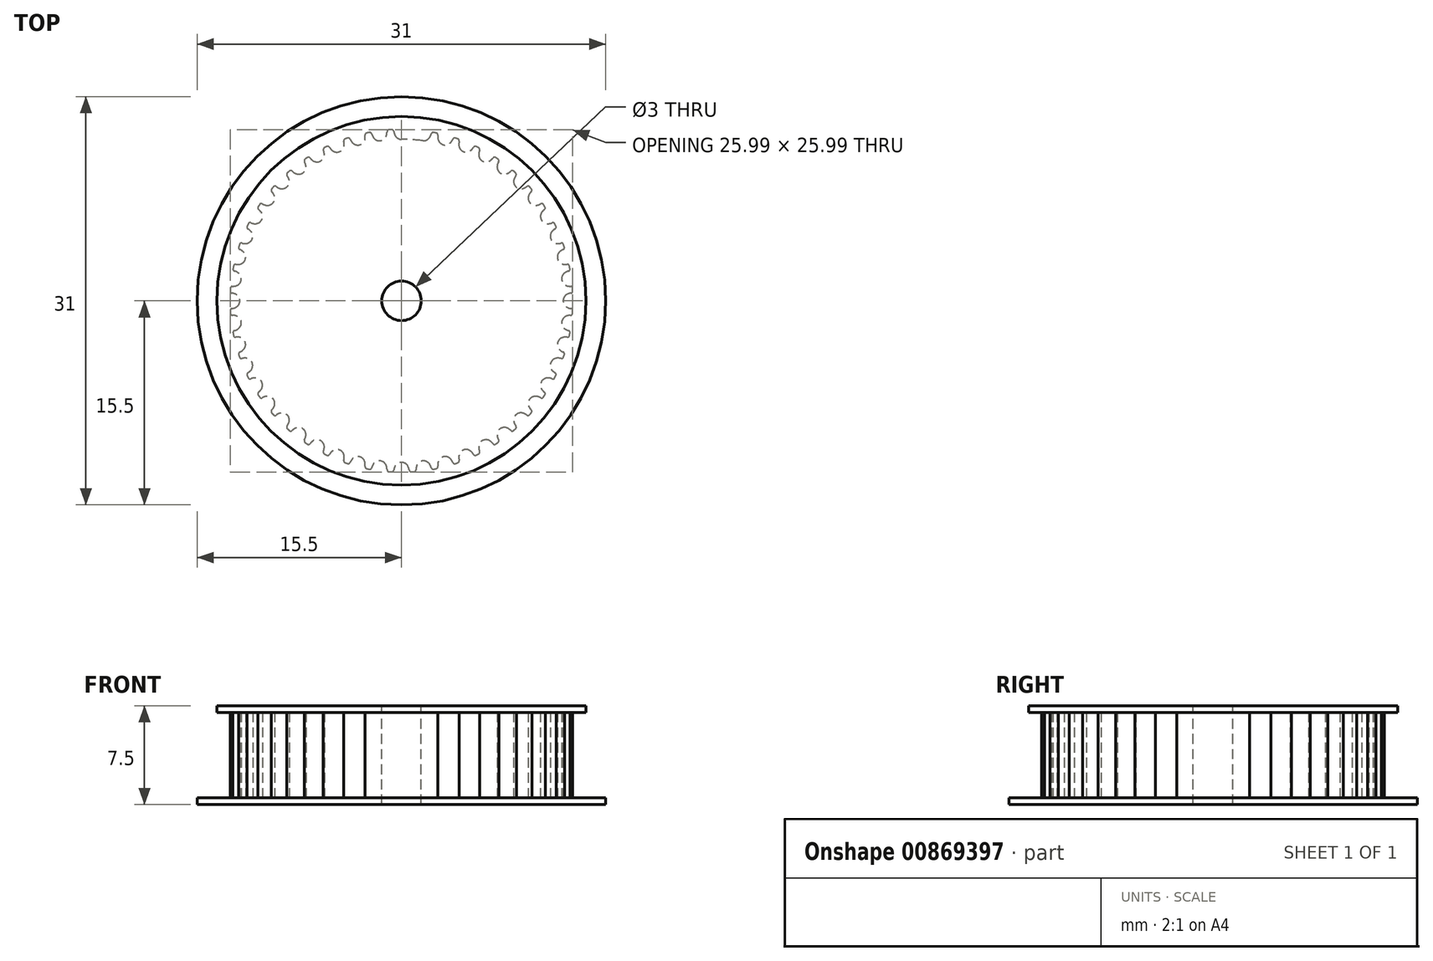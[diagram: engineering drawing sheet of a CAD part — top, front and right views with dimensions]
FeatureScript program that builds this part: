
annotation { "Feature Type Name" : "Feature", "Feature Type Description" : "" }
export const myFeature = defineFeature(function(context is Context, id is Id, definition is map)
    precondition{}
    {
        {
            var Q0;
            Q0=qCreatedBy(makeId("Top.planeOp"),FACE);
            var sketch = newSketch(context, id + "F0", { "sketchPlane" : qUnion([Q0])});
            skArc(sketch, "E0", {"start": v(-0.74, 13) * mm, "mid": v(-0.85, 12.99) * mm, "end": v(-0.96, 12.98) * mm});
            skCircle(sketch, "E1", {"center": v(0, 0) * mm, "radius": 12.27 * mm});
            skArc(sketch, "E2", {"start": v(-0.5, 12.58) * mm, "mid": v(-0.3, 12.35) * mm, "end": v(0, 12.27) * mm});
            skLineSegment(sketch, "E3", {"start": v(0, 0) * mm, "end": v(0.38, 12.26) * mm});
            skArc(sketch, "E4", {"start": v(-0.59, 12.87) * mm, "mid": v(-0.55, 12.72) * mm, "end": v(-0.5, 12.58) * mm});
            skArc(sketch, "E5", {"start": v(-0.59, 12.87) * mm, "mid": v(-0.64, 12.96) * mm, "end": v(-0.74, 13) * mm});
            skArc(sketch, "E6.MirrorCS", {"start": v(0.59, 12.87) * mm, "mid": v(0.64, 12.96) * mm, "end": v(0.74, 13) * mm});
            skArc(sketch, "E7.MirrorCS", {"start": v(0.59, 12.87) * mm, "mid": v(0.55, 12.72) * mm, "end": v(0.5, 12.58) * mm});
            skArc(sketch, "E8.MirrorCS", {"start": v(0.5, 12.58) * mm, "mid": v(0.3, 12.35) * mm, "end": v(0, 12.27) * mm});
            skArc(sketch, "E9.1.0", {"start": v(-2.26, 12.68) * mm, "mid": v(-2.33, 12.77) * mm, "end": v(-2.43, 12.79) * mm});
            skArc(sketch, "E9.1.1", {"start": v(-2.26, 12.68) * mm, "mid": v(-2.21, 12.54) * mm, "end": v(-2.14, 12.41) * mm});
            skArc(sketch, "E9.1.2", {"start": v(-2.14, 12.41) * mm, "mid": v(-1.9, 12.2) * mm, "end": v(-1.6, 12.16) * mm});
            skArc(sketch, "E9.1.3", {"start": v(-1.14, 12.54) * mm, "mid": v(-1.32, 12.28) * mm, "end": v(-1.6, 12.16) * mm});
            skArc(sketch, "E9.1.4", {"start": v(-1.1, 12.83) * mm, "mid": v(-1.11, 12.69) * mm, "end": v(-1.14, 12.54) * mm});
            skArc(sketch, "E9.1.5", {"start": v(-1.1, 12.83) * mm, "mid": v(-1.06, 12.93) * mm, "end": v(-0.96, 12.98) * mm});
            skArc(sketch, "E9.2.0", {"start": v(-3.9, 12.28) * mm, "mid": v(-3.97, 12.35) * mm, "end": v(-4.08, 12.36) * mm});
            skArc(sketch, "E9.2.1", {"start": v(-3.9, 12.28) * mm, "mid": v(-3.83, 12.14) * mm, "end": v(-3.74, 12.03) * mm});
            skArc(sketch, "E9.2.2", {"start": v(-3.74, 12.03) * mm, "mid": v(-3.48, 11.85) * mm, "end": v(-3.17, 11.85) * mm});
            skArc(sketch, "E9.2.3", {"start": v(-2.77, 12.29) * mm, "mid": v(-2.9, 12) * mm, "end": v(-3.17, 11.85) * mm});
            skArc(sketch, "E9.2.4", {"start": v(-2.76, 12.58) * mm, "mid": v(-2.76, 12.43) * mm, "end": v(-2.77, 12.29) * mm});
            skArc(sketch, "E9.2.5", {"start": v(-2.76, 12.58) * mm, "mid": v(-2.74, 12.68) * mm, "end": v(-2.64, 12.74) * mm});
            skArc(sketch, "E9.3.0", {"start": v(-5.47, 11.66) * mm, "mid": v(-5.55, 11.73) * mm, "end": v(-5.66, 11.72) * mm});
            skArc(sketch, "E9.3.1", {"start": v(-5.47, 11.66) * mm, "mid": v(-5.38, 11.54) * mm, "end": v(-5.28, 11.43) * mm});
            skArc(sketch, "E9.3.2", {"start": v(-5.28, 11.43) * mm, "mid": v(-5, 11.3) * mm, "end": v(-4.7, 11.33) * mm});
            skArc(sketch, "E9.3.3", {"start": v(-4.35, 11.82) * mm, "mid": v(-4.45, 11.53) * mm, "end": v(-4.7, 11.33) * mm});
            skArc(sketch, "E9.3.4", {"start": v(-4.38, 12.11) * mm, "mid": v(-4.36, 11.97) * mm, "end": v(-4.35, 11.82) * mm});
            skArc(sketch, "E9.3.5", {"start": v(-4.38, 12.11) * mm, "mid": v(-4.37, 12.22) * mm, "end": v(-4.29, 12.29) * mm});
            skArc(sketch, "E9.4.0", {"start": v(-6.94, 10.85) * mm, "mid": v(-7.03, 10.9) * mm, "end": v(-7.14, 10.88) * mm});
            skArc(sketch, "E9.4.1", {"start": v(-6.94, 10.85) * mm, "mid": v(-6.84, 10.74) * mm, "end": v(-6.73, 10.65) * mm});
            skArc(sketch, "E9.4.2", {"start": v(-6.73, 10.65) * mm, "mid": v(-6.43, 10.55) * mm, "end": v(-6.13, 10.62) * mm});
            skArc(sketch, "E9.4.3", {"start": v(-5.86, 11.15) * mm, "mid": v(-5.92, 10.85) * mm, "end": v(-6.13, 10.62) * mm});
            skArc(sketch, "E9.4.4", {"start": v(-5.92, 11.44) * mm, "mid": v(-5.88, 11.3) * mm, "end": v(-5.86, 11.15) * mm});
            skArc(sketch, "E9.4.5", {"start": v(-5.92, 11.44) * mm, "mid": v(-5.93, 11.54) * mm, "end": v(-5.85, 11.62) * mm});
            skArc(sketch, "E9.5.0", {"start": v(-8.3, 9.85) * mm, "mid": v(-8.4, 9.9) * mm, "end": v(-8.5, 9.86) * mm});
            skArc(sketch, "E9.5.1", {"start": v(-8.3, 9.85) * mm, "mid": v(-8.18, 9.76) * mm, "end": v(-8.06, 9.68) * mm});
            skArc(sketch, "E9.5.2", {"start": v(-8.06, 9.68) * mm, "mid": v(-7.76, 9.62) * mm, "end": v(-7.47, 9.73) * mm});
            skArc(sketch, "E9.5.3", {"start": v(-7.26, 10.29) * mm, "mid": v(-7.28, 9.98) * mm, "end": v(-7.47, 9.73) * mm});
            skArc(sketch, "E9.5.4", {"start": v(-7.37, 10.56) * mm, "mid": v(-7.3, 10.43) * mm, "end": v(-7.26, 10.29) * mm});
            skArc(sketch, "E9.5.5", {"start": v(-7.37, 10.56) * mm, "mid": v(-7.38, 10.67) * mm, "end": v(-7.32, 10.76) * mm});
            skArc(sketch, "E9.6.0", {"start": v(-9.51, 8.68) * mm, "mid": v(-9.62, 8.71) * mm, "end": v(-9.71, 8.66) * mm});
            skArc(sketch, "E9.6.1", {"start": v(-9.51, 8.68) * mm, "mid": v(-9.39, 8.6) * mm, "end": v(-9.25, 8.54) * mm});
            skArc(sketch, "E9.6.2", {"start": v(-9.25, 8.54) * mm, "mid": v(-8.94, 8.52) * mm, "end": v(-8.67, 8.67) * mm});
            skArc(sketch, "E9.6.3", {"start": v(-8.54, 9.25) * mm, "mid": v(-8.52, 8.94) * mm, "end": v(-8.67, 8.67) * mm});
            skArc(sketch, "E9.6.4", {"start": v(-8.68, 9.51) * mm, "mid": v(-8.6, 9.39) * mm, "end": v(-8.54, 9.25) * mm});
            skArc(sketch, "E9.6.5", {"start": v(-8.68, 9.51) * mm, "mid": v(-8.71, 9.62) * mm, "end": v(-8.66, 9.71) * mm});
            skArc(sketch, "E9.7.0", {"start": v(-10.56, 7.37) * mm, "mid": v(-10.67, 7.38) * mm, "end": v(-10.76, 7.32) * mm});
            skArc(sketch, "E9.7.1", {"start": v(-10.56, 7.37) * mm, "mid": v(-10.43, 7.3) * mm, "end": v(-10.29, 7.26) * mm});
            skArc(sketch, "E9.7.2", {"start": v(-10.29, 7.26) * mm, "mid": v(-9.98, 7.28) * mm, "end": v(-9.73, 7.47) * mm});
            skArc(sketch, "E9.7.3", {"start": v(-9.68, 8.06) * mm, "mid": v(-9.62, 7.76) * mm, "end": v(-9.73, 7.47) * mm});
            skArc(sketch, "E9.7.4", {"start": v(-9.85, 8.3) * mm, "mid": v(-9.76, 8.18) * mm, "end": v(-9.68, 8.06) * mm});
            skArc(sketch, "E9.7.5", {"start": v(-9.85, 8.3) * mm, "mid": v(-9.9, 8.4) * mm, "end": v(-9.86, 8.5) * mm});
            skArc(sketch, "E9.8.0", {"start": v(-11.44, 5.92) * mm, "mid": v(-11.54, 5.93) * mm, "end": v(-11.62, 5.85) * mm});
            skArc(sketch, "E9.8.1", {"start": v(-11.44, 5.92) * mm, "mid": v(-11.3, 5.88) * mm, "end": v(-11.15, 5.86) * mm});
            skArc(sketch, "E9.8.2", {"start": v(-11.15, 5.86) * mm, "mid": v(-10.85, 5.92) * mm, "end": v(-10.62, 6.13) * mm});
            skArc(sketch, "E9.8.3", {"start": v(-10.65, 6.73) * mm, "mid": v(-10.55, 6.43) * mm, "end": v(-10.62, 6.13) * mm});
            skArc(sketch, "E9.8.4", {"start": v(-10.85, 6.94) * mm, "mid": v(-10.74, 6.84) * mm, "end": v(-10.65, 6.73) * mm});
            skArc(sketch, "E9.8.5", {"start": v(-10.85, 6.94) * mm, "mid": v(-10.9, 7.03) * mm, "end": v(-10.88, 7.14) * mm});
            skArc(sketch, "E9.9.0", {"start": v(-12.11, 4.38) * mm, "mid": v(-12.22, 4.37) * mm, "end": v(-12.29, 4.29) * mm});
            skArc(sketch, "E9.9.1", {"start": v(-12.11, 4.38) * mm, "mid": v(-11.97, 4.36) * mm, "end": v(-11.82, 4.35) * mm});
            skArc(sketch, "E9.9.2", {"start": v(-11.82, 4.35) * mm, "mid": v(-11.53, 4.45) * mm, "end": v(-11.33, 4.7) * mm});
            skArc(sketch, "E9.9.3", {"start": v(-11.43, 5.28) * mm, "mid": v(-11.3, 5) * mm, "end": v(-11.33, 4.7) * mm});
            skArc(sketch, "E9.9.4", {"start": v(-11.66, 5.47) * mm, "mid": v(-11.54, 5.38) * mm, "end": v(-11.43, 5.28) * mm});
            skArc(sketch, "E9.9.5", {"start": v(-11.66, 5.47) * mm, "mid": v(-11.73, 5.55) * mm, "end": v(-11.72, 5.66) * mm});
            skArc(sketch, "E9.10.0", {"start": v(-12.58, 2.76) * mm, "mid": v(-12.68, 2.74) * mm, "end": v(-12.74, 2.64) * mm});
            skArc(sketch, "E9.10.1", {"start": v(-12.58, 2.76) * mm, "mid": v(-12.43, 2.76) * mm, "end": v(-12.29, 2.77) * mm});
            skArc(sketch, "E9.10.2", {"start": v(-12.29, 2.77) * mm, "mid": v(-12, 2.9) * mm, "end": v(-11.85, 3.17) * mm});
            skArc(sketch, "E9.10.3", {"start": v(-12.03, 3.74) * mm, "mid": v(-11.85, 3.48) * mm, "end": v(-11.85, 3.17) * mm});
            skArc(sketch, "E9.10.4", {"start": v(-12.28, 3.9) * mm, "mid": v(-12.14, 3.83) * mm, "end": v(-12.03, 3.74) * mm});
            skArc(sketch, "E9.10.5", {"start": v(-12.28, 3.9) * mm, "mid": v(-12.35, 3.97) * mm, "end": v(-12.36, 4.08) * mm});
            skArc(sketch, "E9.11.0", {"start": v(-12.83, 1.1) * mm, "mid": v(-12.93, 1.06) * mm, "end": v(-12.98, 0.96) * mm});
            skArc(sketch, "E9.11.1", {"start": v(-12.83, 1.1) * mm, "mid": v(-12.69, 1.11) * mm, "end": v(-12.54, 1.14) * mm});
            skArc(sketch, "E9.11.2", {"start": v(-12.54, 1.14) * mm, "mid": v(-12.28, 1.32) * mm, "end": v(-12.16, 1.6) * mm});
            skArc(sketch, "E9.11.3", {"start": v(-12.41, 2.14) * mm, "mid": v(-12.2, 1.9) * mm, "end": v(-12.16, 1.6) * mm});
            skArc(sketch, "E9.11.4", {"start": v(-12.68, 2.26) * mm, "mid": v(-12.54, 2.21) * mm, "end": v(-12.41, 2.14) * mm});
            skArc(sketch, "E9.11.5", {"start": v(-12.68, 2.26) * mm, "mid": v(-12.77, 2.33) * mm, "end": v(-12.79, 2.43) * mm});
            skArc(sketch, "E9.12.0", {"start": v(-12.87, -0.59) * mm, "mid": v(-12.96, -0.64) * mm, "end": v(-13, -0.74) * mm});
            skArc(sketch, "E9.12.1", {"start": v(-12.87, -0.59) * mm, "mid": v(-12.72, -0.55) * mm, "end": v(-12.58, -0.5) * mm});
            skArc(sketch, "E9.12.2", {"start": v(-12.58, -0.5) * mm, "mid": v(-12.35, -0.3) * mm, "end": v(-12.27, 0) * mm});
            skArc(sketch, "E9.12.3", {"start": v(-12.58, 0.5) * mm, "mid": v(-12.35, 0.3) * mm, "end": v(-12.27, 0) * mm});
            skArc(sketch, "E9.12.4", {"start": v(-12.87, 0.59) * mm, "mid": v(-12.72, 0.55) * mm, "end": v(-12.58, 0.5) * mm});
            skArc(sketch, "E9.12.5", {"start": v(-12.87, 0.59) * mm, "mid": v(-12.96, 0.64) * mm, "end": v(-13, 0.74) * mm});
            skArc(sketch, "E9.13.0", {"start": v(-12.68, -2.26) * mm, "mid": v(-12.77, -2.33) * mm, "end": v(-12.79, -2.43) * mm});
            skArc(sketch, "E9.13.1", {"start": v(-12.68, -2.26) * mm, "mid": v(-12.54, -2.21) * mm, "end": v(-12.41, -2.14) * mm});
            skArc(sketch, "E9.13.2", {"start": v(-12.41, -2.14) * mm, "mid": v(-12.2, -1.9) * mm, "end": v(-12.16, -1.6) * mm});
            skArc(sketch, "E9.13.3", {"start": v(-12.54, -1.14) * mm, "mid": v(-12.28, -1.32) * mm, "end": v(-12.16, -1.6) * mm});
            skArc(sketch, "E9.13.4", {"start": v(-12.83, -1.1) * mm, "mid": v(-12.69, -1.11) * mm, "end": v(-12.54, -1.14) * mm});
            skArc(sketch, "E9.13.5", {"start": v(-12.83, -1.1) * mm, "mid": v(-12.93, -1.06) * mm, "end": v(-12.98, -0.96) * mm});
            skArc(sketch, "E9.14.0", {"start": v(-12.28, -3.9) * mm, "mid": v(-12.35, -3.97) * mm, "end": v(-12.36, -4.08) * mm});
            skArc(sketch, "E9.14.1", {"start": v(-12.28, -3.9) * mm, "mid": v(-12.14, -3.83) * mm, "end": v(-12.03, -3.74) * mm});
            skArc(sketch, "E9.14.2", {"start": v(-12.03, -3.74) * mm, "mid": v(-11.85, -3.48) * mm, "end": v(-11.85, -3.17) * mm});
            skArc(sketch, "E9.14.3", {"start": v(-12.29, -2.77) * mm, "mid": v(-12, -2.9) * mm, "end": v(-11.85, -3.17) * mm});
            skArc(sketch, "E9.14.4", {"start": v(-12.58, -2.76) * mm, "mid": v(-12.43, -2.76) * mm, "end": v(-12.29, -2.77) * mm});
            skArc(sketch, "E9.14.5", {"start": v(-12.58, -2.76) * mm, "mid": v(-12.68, -2.74) * mm, "end": v(-12.74, -2.64) * mm});
            skArc(sketch, "E9.15.0", {"start": v(-11.66, -5.47) * mm, "mid": v(-11.73, -5.55) * mm, "end": v(-11.72, -5.66) * mm});
            skArc(sketch, "E9.15.1", {"start": v(-11.66, -5.47) * mm, "mid": v(-11.54, -5.38) * mm, "end": v(-11.43, -5.28) * mm});
            skArc(sketch, "E9.15.2", {"start": v(-11.43, -5.28) * mm, "mid": v(-11.3, -5) * mm, "end": v(-11.33, -4.7) * mm});
            skArc(sketch, "E9.15.3", {"start": v(-11.82, -4.35) * mm, "mid": v(-11.53, -4.45) * mm, "end": v(-11.33, -4.7) * mm});
            skArc(sketch, "E9.15.4", {"start": v(-12.11, -4.38) * mm, "mid": v(-11.97, -4.36) * mm, "end": v(-11.82, -4.35) * mm});
            skArc(sketch, "E9.15.5", {"start": v(-12.11, -4.38) * mm, "mid": v(-12.22, -4.37) * mm, "end": v(-12.29, -4.29) * mm});
            skArc(sketch, "E9.16.0", {"start": v(-10.85, -6.94) * mm, "mid": v(-10.9, -7.03) * mm, "end": v(-10.88, -7.14) * mm});
            skArc(sketch, "E9.16.1", {"start": v(-10.85, -6.94) * mm, "mid": v(-10.74, -6.84) * mm, "end": v(-10.65, -6.73) * mm});
            skArc(sketch, "E9.16.2", {"start": v(-10.65, -6.73) * mm, "mid": v(-10.55, -6.43) * mm, "end": v(-10.62, -6.13) * mm});
            skArc(sketch, "E9.16.3", {"start": v(-11.15, -5.86) * mm, "mid": v(-10.85, -5.92) * mm, "end": v(-10.62, -6.13) * mm});
            skArc(sketch, "E9.16.4", {"start": v(-11.44, -5.92) * mm, "mid": v(-11.3, -5.88) * mm, "end": v(-11.15, -5.86) * mm});
            skArc(sketch, "E9.16.5", {"start": v(-11.44, -5.92) * mm, "mid": v(-11.54, -5.93) * mm, "end": v(-11.62, -5.85) * mm});
            skArc(sketch, "E9.17.0", {"start": v(-9.85, -8.3) * mm, "mid": v(-9.9, -8.4) * mm, "end": v(-9.86, -8.5) * mm});
            skArc(sketch, "E9.17.1", {"start": v(-9.85, -8.3) * mm, "mid": v(-9.76, -8.18) * mm, "end": v(-9.68, -8.06) * mm});
            skArc(sketch, "E9.17.2", {"start": v(-9.68, -8.06) * mm, "mid": v(-9.62, -7.76) * mm, "end": v(-9.73, -7.47) * mm});
            skArc(sketch, "E9.17.3", {"start": v(-10.29, -7.26) * mm, "mid": v(-9.98, -7.28) * mm, "end": v(-9.73, -7.47) * mm});
            skArc(sketch, "E9.17.4", {"start": v(-10.56, -7.37) * mm, "mid": v(-10.43, -7.3) * mm, "end": v(-10.29, -7.26) * mm});
            skArc(sketch, "E9.17.5", {"start": v(-10.56, -7.37) * mm, "mid": v(-10.67, -7.38) * mm, "end": v(-10.76, -7.32) * mm});
            skArc(sketch, "E9.18.0", {"start": v(-8.68, -9.51) * mm, "mid": v(-8.71, -9.62) * mm, "end": v(-8.66, -9.71) * mm});
            skArc(sketch, "E9.18.1", {"start": v(-8.68, -9.51) * mm, "mid": v(-8.6, -9.39) * mm, "end": v(-8.54, -9.25) * mm});
            skArc(sketch, "E9.18.2", {"start": v(-8.54, -9.25) * mm, "mid": v(-8.52, -8.94) * mm, "end": v(-8.67, -8.67) * mm});
            skArc(sketch, "E9.18.3", {"start": v(-9.25, -8.54) * mm, "mid": v(-8.94, -8.52) * mm, "end": v(-8.67, -8.67) * mm});
            skArc(sketch, "E9.18.4", {"start": v(-9.51, -8.68) * mm, "mid": v(-9.39, -8.6) * mm, "end": v(-9.25, -8.54) * mm});
            skArc(sketch, "E9.18.5", {"start": v(-9.51, -8.68) * mm, "mid": v(-9.62, -8.71) * mm, "end": v(-9.71, -8.66) * mm});
            skArc(sketch, "E9.19.0", {"start": v(-7.37, -10.56) * mm, "mid": v(-7.38, -10.67) * mm, "end": v(-7.32, -10.76) * mm});
            skArc(sketch, "E9.19.1", {"start": v(-7.37, -10.56) * mm, "mid": v(-7.3, -10.43) * mm, "end": v(-7.26, -10.29) * mm});
            skArc(sketch, "E9.19.2", {"start": v(-7.26, -10.29) * mm, "mid": v(-7.28, -9.98) * mm, "end": v(-7.47, -9.73) * mm});
            skArc(sketch, "E9.19.3", {"start": v(-8.06, -9.68) * mm, "mid": v(-7.76, -9.62) * mm, "end": v(-7.47, -9.73) * mm});
            skArc(sketch, "E9.19.4", {"start": v(-8.3, -9.85) * mm, "mid": v(-8.18, -9.76) * mm, "end": v(-8.06, -9.68) * mm});
            skArc(sketch, "E9.19.5", {"start": v(-8.3, -9.85) * mm, "mid": v(-8.4, -9.9) * mm, "end": v(-8.5, -9.86) * mm});
            skArc(sketch, "E9.20.0", {"start": v(-5.92, -11.44) * mm, "mid": v(-5.93, -11.54) * mm, "end": v(-5.85, -11.62) * mm});
            skArc(sketch, "E9.20.1", {"start": v(-5.92, -11.44) * mm, "mid": v(-5.88, -11.3) * mm, "end": v(-5.86, -11.15) * mm});
            skArc(sketch, "E9.20.2", {"start": v(-5.86, -11.15) * mm, "mid": v(-5.92, -10.85) * mm, "end": v(-6.13, -10.62) * mm});
            skArc(sketch, "E9.20.3", {"start": v(-6.73, -10.65) * mm, "mid": v(-6.43, -10.55) * mm, "end": v(-6.13, -10.62) * mm});
            skArc(sketch, "E9.20.4", {"start": v(-6.94, -10.85) * mm, "mid": v(-6.84, -10.74) * mm, "end": v(-6.73, -10.65) * mm});
            skArc(sketch, "E9.20.5", {"start": v(-6.94, -10.85) * mm, "mid": v(-7.03, -10.9) * mm, "end": v(-7.14, -10.88) * mm});
            skArc(sketch, "E9.21.0", {"start": v(-4.38, -12.11) * mm, "mid": v(-4.37, -12.22) * mm, "end": v(-4.29, -12.29) * mm});
            skArc(sketch, "E9.21.1", {"start": v(-4.38, -12.11) * mm, "mid": v(-4.36, -11.97) * mm, "end": v(-4.35, -11.82) * mm});
            skArc(sketch, "E9.21.2", {"start": v(-4.35, -11.82) * mm, "mid": v(-4.45, -11.53) * mm, "end": v(-4.7, -11.33) * mm});
            skArc(sketch, "E9.21.3", {"start": v(-5.28, -11.43) * mm, "mid": v(-5, -11.3) * mm, "end": v(-4.7, -11.33) * mm});
            skArc(sketch, "E9.21.4", {"start": v(-5.47, -11.66) * mm, "mid": v(-5.38, -11.54) * mm, "end": v(-5.28, -11.43) * mm});
            skArc(sketch, "E9.21.5", {"start": v(-5.47, -11.66) * mm, "mid": v(-5.55, -11.73) * mm, "end": v(-5.66, -11.72) * mm});
            skArc(sketch, "E9.22.0", {"start": v(-2.76, -12.58) * mm, "mid": v(-2.74, -12.68) * mm, "end": v(-2.64, -12.74) * mm});
            skArc(sketch, "E9.22.1", {"start": v(-2.76, -12.58) * mm, "mid": v(-2.76, -12.43) * mm, "end": v(-2.77, -12.29) * mm});
            skArc(sketch, "E9.22.2", {"start": v(-2.77, -12.29) * mm, "mid": v(-2.9, -12) * mm, "end": v(-3.17, -11.85) * mm});
            skArc(sketch, "E9.22.3", {"start": v(-3.74, -12.03) * mm, "mid": v(-3.48, -11.85) * mm, "end": v(-3.17, -11.85) * mm});
            skArc(sketch, "E9.22.4", {"start": v(-3.9, -12.28) * mm, "mid": v(-3.83, -12.14) * mm, "end": v(-3.74, -12.03) * mm});
            skArc(sketch, "E9.22.5", {"start": v(-3.9, -12.28) * mm, "mid": v(-3.97, -12.35) * mm, "end": v(-4.08, -12.36) * mm});
            skArc(sketch, "E9.23.0", {"start": v(-1.1, -12.83) * mm, "mid": v(-1.06, -12.93) * mm, "end": v(-0.96, -12.98) * mm});
            skArc(sketch, "E9.23.1", {"start": v(-1.1, -12.83) * mm, "mid": v(-1.11, -12.69) * mm, "end": v(-1.14, -12.54) * mm});
            skArc(sketch, "E9.23.2", {"start": v(-1.14, -12.54) * mm, "mid": v(-1.32, -12.28) * mm, "end": v(-1.6, -12.16) * mm});
            skArc(sketch, "E9.23.3", {"start": v(-2.14, -12.41) * mm, "mid": v(-1.9, -12.2) * mm, "end": v(-1.6, -12.16) * mm});
            skArc(sketch, "E9.23.4", {"start": v(-2.26, -12.68) * mm, "mid": v(-2.21, -12.54) * mm, "end": v(-2.14, -12.41) * mm});
            skArc(sketch, "E9.23.5", {"start": v(-2.26, -12.68) * mm, "mid": v(-2.33, -12.77) * mm, "end": v(-2.43, -12.79) * mm});
            skArc(sketch, "E9.24.0", {"start": v(0.59, -12.87) * mm, "mid": v(0.64, -12.96) * mm, "end": v(0.74, -13) * mm});
            skArc(sketch, "E9.24.1", {"start": v(0.59, -12.87) * mm, "mid": v(0.55, -12.72) * mm, "end": v(0.5, -12.58) * mm});
            skArc(sketch, "E9.24.2", {"start": v(0.5, -12.58) * mm, "mid": v(0.3, -12.35) * mm, "end": v(0, -12.27) * mm});
            skArc(sketch, "E9.24.3", {"start": v(-0.5, -12.58) * mm, "mid": v(-0.3, -12.35) * mm, "end": v(0, -12.27) * mm});
            skArc(sketch, "E9.24.4", {"start": v(-0.59, -12.87) * mm, "mid": v(-0.55, -12.72) * mm, "end": v(-0.5, -12.58) * mm});
            skArc(sketch, "E9.24.5", {"start": v(-0.59, -12.87) * mm, "mid": v(-0.64, -12.96) * mm, "end": v(-0.74, -13) * mm});
            skArc(sketch, "E9.25.0", {"start": v(2.26, -12.68) * mm, "mid": v(2.33, -12.77) * mm, "end": v(2.43, -12.79) * mm});
            skArc(sketch, "E9.25.1", {"start": v(2.26, -12.68) * mm, "mid": v(2.21, -12.54) * mm, "end": v(2.14, -12.41) * mm});
            skArc(sketch, "E9.25.2", {"start": v(2.14, -12.41) * mm, "mid": v(1.9, -12.2) * mm, "end": v(1.6, -12.16) * mm});
            skArc(sketch, "E9.25.3", {"start": v(1.14, -12.54) * mm, "mid": v(1.32, -12.28) * mm, "end": v(1.6, -12.16) * mm});
            skArc(sketch, "E9.25.4", {"start": v(1.1, -12.83) * mm, "mid": v(1.11, -12.69) * mm, "end": v(1.14, -12.54) * mm});
            skArc(sketch, "E9.25.5", {"start": v(1.1, -12.83) * mm, "mid": v(1.06, -12.93) * mm, "end": v(0.96, -12.98) * mm});
            skArc(sketch, "E9.26.0", {"start": v(3.9, -12.28) * mm, "mid": v(3.97, -12.35) * mm, "end": v(4.08, -12.36) * mm});
            skArc(sketch, "E9.26.1", {"start": v(3.9, -12.28) * mm, "mid": v(3.83, -12.14) * mm, "end": v(3.74, -12.03) * mm});
            skArc(sketch, "E9.26.2", {"start": v(3.74, -12.03) * mm, "mid": v(3.48, -11.85) * mm, "end": v(3.17, -11.85) * mm});
            skArc(sketch, "E9.26.3", {"start": v(2.77, -12.29) * mm, "mid": v(2.9, -12) * mm, "end": v(3.17, -11.85) * mm});
            skArc(sketch, "E9.26.4", {"start": v(2.76, -12.58) * mm, "mid": v(2.76, -12.43) * mm, "end": v(2.77, -12.29) * mm});
            skArc(sketch, "E9.26.5", {"start": v(2.76, -12.58) * mm, "mid": v(2.74, -12.68) * mm, "end": v(2.64, -12.74) * mm});
            skArc(sketch, "E9.27.0", {"start": v(5.47, -11.66) * mm, "mid": v(5.55, -11.73) * mm, "end": v(5.66, -11.72) * mm});
            skArc(sketch, "E9.27.1", {"start": v(5.47, -11.66) * mm, "mid": v(5.38, -11.54) * mm, "end": v(5.28, -11.43) * mm});
            skArc(sketch, "E9.27.2", {"start": v(5.28, -11.43) * mm, "mid": v(5, -11.3) * mm, "end": v(4.7, -11.33) * mm});
            skArc(sketch, "E9.27.3", {"start": v(4.35, -11.82) * mm, "mid": v(4.45, -11.53) * mm, "end": v(4.7, -11.33) * mm});
            skArc(sketch, "E9.27.4", {"start": v(4.38, -12.11) * mm, "mid": v(4.36, -11.97) * mm, "end": v(4.35, -11.82) * mm});
            skArc(sketch, "E9.27.5", {"start": v(4.38, -12.11) * mm, "mid": v(4.37, -12.22) * mm, "end": v(4.29, -12.29) * mm});
            skArc(sketch, "E9.28.0", {"start": v(6.94, -10.85) * mm, "mid": v(7.03, -10.9) * mm, "end": v(7.14, -10.88) * mm});
            skArc(sketch, "E9.28.1", {"start": v(6.94, -10.85) * mm, "mid": v(6.84, -10.74) * mm, "end": v(6.73, -10.65) * mm});
            skArc(sketch, "E9.28.2", {"start": v(6.73, -10.65) * mm, "mid": v(6.43, -10.55) * mm, "end": v(6.13, -10.62) * mm});
            skArc(sketch, "E9.28.3", {"start": v(5.86, -11.15) * mm, "mid": v(5.92, -10.85) * mm, "end": v(6.13, -10.62) * mm});
            skArc(sketch, "E9.28.4", {"start": v(5.92, -11.44) * mm, "mid": v(5.88, -11.3) * mm, "end": v(5.86, -11.15) * mm});
            skArc(sketch, "E9.28.5", {"start": v(5.92, -11.44) * mm, "mid": v(5.93, -11.54) * mm, "end": v(5.85, -11.62) * mm});
            skArc(sketch, "E9.29.0", {"start": v(8.3, -9.85) * mm, "mid": v(8.4, -9.9) * mm, "end": v(8.5, -9.86) * mm});
            skArc(sketch, "E9.29.1", {"start": v(8.3, -9.85) * mm, "mid": v(8.18, -9.76) * mm, "end": v(8.06, -9.68) * mm});
            skArc(sketch, "E9.29.2", {"start": v(8.06, -9.68) * mm, "mid": v(7.76, -9.62) * mm, "end": v(7.47, -9.73) * mm});
            skArc(sketch, "E9.29.3", {"start": v(7.26, -10.29) * mm, "mid": v(7.28, -9.98) * mm, "end": v(7.47, -9.73) * mm});
            skArc(sketch, "E9.29.4", {"start": v(7.37, -10.56) * mm, "mid": v(7.3, -10.43) * mm, "end": v(7.26, -10.29) * mm});
            skArc(sketch, "E9.29.5", {"start": v(7.37, -10.56) * mm, "mid": v(7.38, -10.67) * mm, "end": v(7.32, -10.76) * mm});
            skArc(sketch, "E9.30.0", {"start": v(9.51, -8.68) * mm, "mid": v(9.62, -8.71) * mm, "end": v(9.71, -8.66) * mm});
            skArc(sketch, "E9.30.1", {"start": v(9.51, -8.68) * mm, "mid": v(9.39, -8.6) * mm, "end": v(9.25, -8.54) * mm});
            skArc(sketch, "E9.30.2", {"start": v(9.25, -8.54) * mm, "mid": v(8.94, -8.52) * mm, "end": v(8.67, -8.67) * mm});
            skArc(sketch, "E9.30.3", {"start": v(8.54, -9.25) * mm, "mid": v(8.52, -8.94) * mm, "end": v(8.67, -8.67) * mm});
            skArc(sketch, "E9.30.4", {"start": v(8.68, -9.51) * mm, "mid": v(8.6, -9.39) * mm, "end": v(8.54, -9.25) * mm});
            skArc(sketch, "E9.30.5", {"start": v(8.68, -9.51) * mm, "mid": v(8.71, -9.62) * mm, "end": v(8.66, -9.71) * mm});
            skArc(sketch, "E9.31.0", {"start": v(10.56, -7.37) * mm, "mid": v(10.67, -7.38) * mm, "end": v(10.76, -7.32) * mm});
            skArc(sketch, "E9.31.1", {"start": v(10.56, -7.37) * mm, "mid": v(10.43, -7.3) * mm, "end": v(10.29, -7.26) * mm});
            skArc(sketch, "E9.31.2", {"start": v(10.29, -7.26) * mm, "mid": v(9.98, -7.28) * mm, "end": v(9.73, -7.47) * mm});
            skArc(sketch, "E9.31.3", {"start": v(9.68, -8.06) * mm, "mid": v(9.62, -7.76) * mm, "end": v(9.73, -7.47) * mm});
            skArc(sketch, "E9.31.4", {"start": v(9.85, -8.3) * mm, "mid": v(9.76, -8.18) * mm, "end": v(9.68, -8.06) * mm});
            skArc(sketch, "E9.31.5", {"start": v(9.85, -8.3) * mm, "mid": v(9.9, -8.4) * mm, "end": v(9.86, -8.5) * mm});
            skArc(sketch, "E9.32.0", {"start": v(11.44, -5.92) * mm, "mid": v(11.54, -5.93) * mm, "end": v(11.62, -5.85) * mm});
            skArc(sketch, "E9.32.1", {"start": v(11.44, -5.92) * mm, "mid": v(11.3, -5.88) * mm, "end": v(11.15, -5.86) * mm});
            skArc(sketch, "E9.32.2", {"start": v(11.15, -5.86) * mm, "mid": v(10.85, -5.92) * mm, "end": v(10.62, -6.13) * mm});
            skArc(sketch, "E9.32.3", {"start": v(10.65, -6.73) * mm, "mid": v(10.55, -6.43) * mm, "end": v(10.62, -6.13) * mm});
            skArc(sketch, "E9.32.4", {"start": v(10.85, -6.94) * mm, "mid": v(10.74, -6.84) * mm, "end": v(10.65, -6.73) * mm});
            skArc(sketch, "E9.32.5", {"start": v(10.85, -6.94) * mm, "mid": v(10.9, -7.03) * mm, "end": v(10.88, -7.14) * mm});
            skArc(sketch, "E9.33.0", {"start": v(12.11, -4.38) * mm, "mid": v(12.22, -4.37) * mm, "end": v(12.29, -4.29) * mm});
            skArc(sketch, "E9.33.1", {"start": v(12.11, -4.38) * mm, "mid": v(11.97, -4.36) * mm, "end": v(11.82, -4.35) * mm});
            skArc(sketch, "E9.33.2", {"start": v(11.82, -4.35) * mm, "mid": v(11.53, -4.45) * mm, "end": v(11.33, -4.7) * mm});
            skArc(sketch, "E9.33.3", {"start": v(11.43, -5.28) * mm, "mid": v(11.3, -5) * mm, "end": v(11.33, -4.7) * mm});
            skArc(sketch, "E9.33.4", {"start": v(11.66, -5.47) * mm, "mid": v(11.54, -5.38) * mm, "end": v(11.43, -5.28) * mm});
            skArc(sketch, "E9.33.5", {"start": v(11.66, -5.47) * mm, "mid": v(11.73, -5.55) * mm, "end": v(11.72, -5.66) * mm});
            skArc(sketch, "E9.34.0", {"start": v(12.58, -2.76) * mm, "mid": v(12.68, -2.74) * mm, "end": v(12.74, -2.64) * mm});
            skArc(sketch, "E9.34.1", {"start": v(12.58, -2.76) * mm, "mid": v(12.43, -2.76) * mm, "end": v(12.29, -2.77) * mm});
            skArc(sketch, "E9.34.2", {"start": v(12.29, -2.77) * mm, "mid": v(12, -2.9) * mm, "end": v(11.85, -3.17) * mm});
            skArc(sketch, "E9.34.3", {"start": v(12.03, -3.74) * mm, "mid": v(11.85, -3.48) * mm, "end": v(11.85, -3.17) * mm});
            skArc(sketch, "E9.34.4", {"start": v(12.28, -3.9) * mm, "mid": v(12.14, -3.83) * mm, "end": v(12.03, -3.74) * mm});
            skArc(sketch, "E9.34.5", {"start": v(12.28, -3.9) * mm, "mid": v(12.35, -3.97) * mm, "end": v(12.36, -4.08) * mm});
            skArc(sketch, "E9.35.0", {"start": v(12.83, -1.1) * mm, "mid": v(12.93, -1.06) * mm, "end": v(12.98, -0.96) * mm});
            skArc(sketch, "E9.35.1", {"start": v(12.83, -1.1) * mm, "mid": v(12.69, -1.11) * mm, "end": v(12.54, -1.14) * mm});
            skArc(sketch, "E9.35.2", {"start": v(12.54, -1.14) * mm, "mid": v(12.28, -1.32) * mm, "end": v(12.16, -1.6) * mm});
            skArc(sketch, "E9.35.3", {"start": v(12.41, -2.14) * mm, "mid": v(12.2, -1.9) * mm, "end": v(12.16, -1.6) * mm});
            skArc(sketch, "E9.35.4", {"start": v(12.68, -2.26) * mm, "mid": v(12.54, -2.21) * mm, "end": v(12.41, -2.14) * mm});
            skArc(sketch, "E9.35.5", {"start": v(12.68, -2.26) * mm, "mid": v(12.77, -2.33) * mm, "end": v(12.79, -2.43) * mm});
            skArc(sketch, "E9.36.0", {"start": v(12.87, 0.59) * mm, "mid": v(12.96, 0.64) * mm, "end": v(13, 0.74) * mm});
            skArc(sketch, "E9.36.1", {"start": v(12.87, 0.59) * mm, "mid": v(12.72, 0.55) * mm, "end": v(12.58, 0.5) * mm});
            skArc(sketch, "E9.36.2", {"start": v(12.58, 0.5) * mm, "mid": v(12.35, 0.3) * mm, "end": v(12.27, 0) * mm});
            skArc(sketch, "E9.36.3", {"start": v(12.58, -0.5) * mm, "mid": v(12.35, -0.3) * mm, "end": v(12.27, 0) * mm});
            skArc(sketch, "E9.36.4", {"start": v(12.87, -0.59) * mm, "mid": v(12.72, -0.55) * mm, "end": v(12.58, -0.5) * mm});
            skArc(sketch, "E9.36.5", {"start": v(12.87, -0.59) * mm, "mid": v(12.96, -0.64) * mm, "end": v(13, -0.74) * mm});
            skArc(sketch, "E9.37.0", {"start": v(12.68, 2.26) * mm, "mid": v(12.77, 2.33) * mm, "end": v(12.79, 2.43) * mm});
            skArc(sketch, "E9.37.1", {"start": v(12.68, 2.26) * mm, "mid": v(12.54, 2.21) * mm, "end": v(12.41, 2.14) * mm});
            skArc(sketch, "E9.37.2", {"start": v(12.41, 2.14) * mm, "mid": v(12.2, 1.9) * mm, "end": v(12.16, 1.6) * mm});
            skArc(sketch, "E9.37.3", {"start": v(12.54, 1.14) * mm, "mid": v(12.28, 1.32) * mm, "end": v(12.16, 1.6) * mm});
            skArc(sketch, "E9.37.4", {"start": v(12.83, 1.1) * mm, "mid": v(12.69, 1.11) * mm, "end": v(12.54, 1.14) * mm});
            skArc(sketch, "E9.37.5", {"start": v(12.83, 1.1) * mm, "mid": v(12.93, 1.06) * mm, "end": v(12.98, 0.96) * mm});
            skArc(sketch, "E9.38.0", {"start": v(12.28, 3.9) * mm, "mid": v(12.35, 3.97) * mm, "end": v(12.36, 4.08) * mm});
            skArc(sketch, "E9.38.1", {"start": v(12.28, 3.9) * mm, "mid": v(12.14, 3.83) * mm, "end": v(12.03, 3.74) * mm});
            skArc(sketch, "E9.38.2", {"start": v(12.03, 3.74) * mm, "mid": v(11.85, 3.48) * mm, "end": v(11.85, 3.17) * mm});
            skArc(sketch, "E9.38.3", {"start": v(12.29, 2.77) * mm, "mid": v(12, 2.9) * mm, "end": v(11.85, 3.17) * mm});
            skArc(sketch, "E9.38.4", {"start": v(12.58, 2.76) * mm, "mid": v(12.43, 2.76) * mm, "end": v(12.29, 2.77) * mm});
            skArc(sketch, "E9.38.5", {"start": v(12.58, 2.76) * mm, "mid": v(12.68, 2.74) * mm, "end": v(12.74, 2.64) * mm});
            skArc(sketch, "E9.39.0", {"start": v(11.66, 5.47) * mm, "mid": v(11.73, 5.55) * mm, "end": v(11.72, 5.66) * mm});
            skArc(sketch, "E9.39.1", {"start": v(11.66, 5.47) * mm, "mid": v(11.54, 5.38) * mm, "end": v(11.43, 5.28) * mm});
            skArc(sketch, "E9.39.2", {"start": v(11.43, 5.28) * mm, "mid": v(11.3, 5) * mm, "end": v(11.33, 4.7) * mm});
            skArc(sketch, "E9.39.3", {"start": v(11.82, 4.35) * mm, "mid": v(11.53, 4.45) * mm, "end": v(11.33, 4.7) * mm});
            skArc(sketch, "E9.39.4", {"start": v(12.11, 4.38) * mm, "mid": v(11.97, 4.36) * mm, "end": v(11.82, 4.35) * mm});
            skArc(sketch, "E9.39.5", {"start": v(12.11, 4.38) * mm, "mid": v(12.22, 4.37) * mm, "end": v(12.29, 4.29) * mm});
            skArc(sketch, "E9.40.0", {"start": v(10.85, 6.94) * mm, "mid": v(10.9, 7.03) * mm, "end": v(10.88, 7.14) * mm});
            skArc(sketch, "E9.40.1", {"start": v(10.85, 6.94) * mm, "mid": v(10.74, 6.84) * mm, "end": v(10.65, 6.73) * mm});
            skArc(sketch, "E9.40.2", {"start": v(10.65, 6.73) * mm, "mid": v(10.55, 6.43) * mm, "end": v(10.62, 6.13) * mm});
            skArc(sketch, "E9.40.3", {"start": v(11.15, 5.86) * mm, "mid": v(10.85, 5.92) * mm, "end": v(10.62, 6.13) * mm});
            skArc(sketch, "E9.40.4", {"start": v(11.44, 5.92) * mm, "mid": v(11.3, 5.88) * mm, "end": v(11.15, 5.86) * mm});
            skArc(sketch, "E9.40.5", {"start": v(11.44, 5.92) * mm, "mid": v(11.54, 5.93) * mm, "end": v(11.62, 5.85) * mm});
            skArc(sketch, "E9.41.0", {"start": v(9.85, 8.3) * mm, "mid": v(9.9, 8.4) * mm, "end": v(9.86, 8.5) * mm});
            skArc(sketch, "E9.41.1", {"start": v(9.85, 8.3) * mm, "mid": v(9.76, 8.18) * mm, "end": v(9.68, 8.06) * mm});
            skArc(sketch, "E9.41.2", {"start": v(9.68, 8.06) * mm, "mid": v(9.62, 7.76) * mm, "end": v(9.73, 7.47) * mm});
            skArc(sketch, "E9.41.3", {"start": v(10.29, 7.26) * mm, "mid": v(9.98, 7.28) * mm, "end": v(9.73, 7.47) * mm});
            skArc(sketch, "E9.41.4", {"start": v(10.56, 7.37) * mm, "mid": v(10.43, 7.3) * mm, "end": v(10.29, 7.26) * mm});
            skArc(sketch, "E9.41.5", {"start": v(10.56, 7.37) * mm, "mid": v(10.67, 7.38) * mm, "end": v(10.76, 7.32) * mm});
            skArc(sketch, "E9.42.0", {"start": v(8.68, 9.51) * mm, "mid": v(8.71, 9.62) * mm, "end": v(8.66, 9.71) * mm});
            skArc(sketch, "E9.42.1", {"start": v(8.68, 9.51) * mm, "mid": v(8.6, 9.39) * mm, "end": v(8.54, 9.25) * mm});
            skArc(sketch, "E9.42.2", {"start": v(8.54, 9.25) * mm, "mid": v(8.52, 8.94) * mm, "end": v(8.67, 8.67) * mm});
            skArc(sketch, "E9.42.3", {"start": v(9.25, 8.54) * mm, "mid": v(8.94, 8.52) * mm, "end": v(8.67, 8.67) * mm});
            skArc(sketch, "E9.42.4", {"start": v(9.51, 8.68) * mm, "mid": v(9.39, 8.6) * mm, "end": v(9.25, 8.54) * mm});
            skArc(sketch, "E9.42.5", {"start": v(9.51, 8.68) * mm, "mid": v(9.62, 8.71) * mm, "end": v(9.71, 8.66) * mm});
            skArc(sketch, "E9.43.0", {"start": v(7.37, 10.56) * mm, "mid": v(7.38, 10.67) * mm, "end": v(7.32, 10.76) * mm});
            skArc(sketch, "E9.43.1", {"start": v(7.37, 10.56) * mm, "mid": v(7.3, 10.43) * mm, "end": v(7.26, 10.29) * mm});
            skArc(sketch, "E9.43.2", {"start": v(7.26, 10.29) * mm, "mid": v(7.28, 9.98) * mm, "end": v(7.47, 9.73) * mm});
            skArc(sketch, "E9.43.3", {"start": v(8.06, 9.68) * mm, "mid": v(7.76, 9.62) * mm, "end": v(7.47, 9.73) * mm});
            skArc(sketch, "E9.43.4", {"start": v(8.3, 9.85) * mm, "mid": v(8.18, 9.76) * mm, "end": v(8.06, 9.68) * mm});
            skArc(sketch, "E9.43.5", {"start": v(8.3, 9.85) * mm, "mid": v(8.4, 9.9) * mm, "end": v(8.5, 9.86) * mm});
            skArc(sketch, "E9.44.0", {"start": v(5.92, 11.44) * mm, "mid": v(5.93, 11.54) * mm, "end": v(5.85, 11.62) * mm});
            skArc(sketch, "E9.44.1", {"start": v(5.92, 11.44) * mm, "mid": v(5.88, 11.3) * mm, "end": v(5.86, 11.15) * mm});
            skArc(sketch, "E9.44.2", {"start": v(5.86, 11.15) * mm, "mid": v(5.92, 10.85) * mm, "end": v(6.13, 10.62) * mm});
            skArc(sketch, "E9.44.3", {"start": v(6.73, 10.65) * mm, "mid": v(6.43, 10.55) * mm, "end": v(6.13, 10.62) * mm});
            skArc(sketch, "E9.44.4", {"start": v(6.94, 10.85) * mm, "mid": v(6.84, 10.74) * mm, "end": v(6.73, 10.65) * mm});
            skArc(sketch, "E9.44.5", {"start": v(6.94, 10.85) * mm, "mid": v(7.03, 10.9) * mm, "end": v(7.14, 10.88) * mm});
            skArc(sketch, "E9.45.0", {"start": v(4.38, 12.11) * mm, "mid": v(4.37, 12.22) * mm, "end": v(4.29, 12.29) * mm});
            skArc(sketch, "E9.45.1", {"start": v(4.38, 12.11) * mm, "mid": v(4.36, 11.97) * mm, "end": v(4.35, 11.82) * mm});
            skArc(sketch, "E9.45.2", {"start": v(4.35, 11.82) * mm, "mid": v(4.45, 11.53) * mm, "end": v(4.7, 11.33) * mm});
            skArc(sketch, "E9.45.3", {"start": v(5.28, 11.43) * mm, "mid": v(5, 11.3) * mm, "end": v(4.7, 11.33) * mm});
            skArc(sketch, "E9.45.4", {"start": v(5.47, 11.66) * mm, "mid": v(5.38, 11.54) * mm, "end": v(5.28, 11.43) * mm});
            skArc(sketch, "E9.45.5", {"start": v(5.47, 11.66) * mm, "mid": v(5.55, 11.73) * mm, "end": v(5.66, 11.72) * mm});
            skArc(sketch, "E9.46.0", {"start": v(2.76, 12.58) * mm, "mid": v(2.74, 12.68) * mm, "end": v(2.64, 12.74) * mm});
            skArc(sketch, "E9.46.1", {"start": v(2.76, 12.58) * mm, "mid": v(2.76, 12.43) * mm, "end": v(2.77, 12.29) * mm});
            skArc(sketch, "E9.46.2", {"start": v(2.77, 12.29) * mm, "mid": v(2.9, 12) * mm, "end": v(3.17, 11.85) * mm});
            skArc(sketch, "E9.46.3", {"start": v(3.74, 12.03) * mm, "mid": v(3.48, 11.85) * mm, "end": v(3.17, 11.85) * mm});
            skArc(sketch, "E9.46.4", {"start": v(3.9, 12.28) * mm, "mid": v(3.83, 12.14) * mm, "end": v(3.74, 12.03) * mm});
            skArc(sketch, "E9.46.5", {"start": v(3.9, 12.28) * mm, "mid": v(3.97, 12.35) * mm, "end": v(4.08, 12.36) * mm});
            skArc(sketch, "E9.47.0", {"start": v(1.1, 12.83) * mm, "mid": v(1.06, 12.93) * mm, "end": v(0.96, 12.98) * mm});
            skArc(sketch, "E9.47.1", {"start": v(1.1, 12.83) * mm, "mid": v(1.11, 12.69) * mm, "end": v(1.14, 12.54) * mm});
            skArc(sketch, "E9.47.2", {"start": v(1.14, 12.54) * mm, "mid": v(1.32, 12.28) * mm, "end": v(1.6, 12.16) * mm});
            skArc(sketch, "E9.47.3", {"start": v(2.14, 12.41) * mm, "mid": v(1.9, 12.2) * mm, "end": v(1.6, 12.16) * mm});
            skArc(sketch, "E9.47.4", {"start": v(2.26, 12.68) * mm, "mid": v(2.21, 12.54) * mm, "end": v(2.14, 12.41) * mm});
            skArc(sketch, "E9.47.5", {"start": v(2.26, 12.68) * mm, "mid": v(2.33, 12.77) * mm, "end": v(2.43, 12.79) * mm});
            skArc(sketch, "E10.trimOffspring", {"start": v(0.96, 12.98) * mm, "mid": v(0.85, 12.99) * mm, "end": v(0.74, 13) * mm});
            skArc(sketch, "E11.trimOffspring", {"start": v(2.64, 12.74) * mm, "mid": v(2.54, 12.76) * mm, "end": v(2.43, 12.79) * mm});
            skArc(sketch, "E12.trimOffspring", {"start": v(4.29, 12.29) * mm, "mid": v(4.18, 12.32) * mm, "end": v(4.08, 12.36) * mm});
            skArc(sketch, "E13.trimOffspring", {"start": v(5.85, 11.62) * mm, "mid": v(5.76, 11.67) * mm, "end": v(5.66, 11.72) * mm});
            skArc(sketch, "E14.trimOffspring", {"start": v(7.32, 10.76) * mm, "mid": v(7.23, 10.82) * mm, "end": v(7.14, 10.88) * mm});
            skArc(sketch, "E15.trimOffspring", {"start": v(8.66, 9.71) * mm, "mid": v(8.58, 9.79) * mm, "end": v(8.5, 9.86) * mm});
            skArc(sketch, "E16.trimOffspring", {"start": v(9.86, 8.5) * mm, "mid": v(9.79, 8.58) * mm, "end": v(9.71, 8.66) * mm});
            skArc(sketch, "E17.trimOffspring", {"start": v(10.88, 7.14) * mm, "mid": v(10.82, 7.23) * mm, "end": v(10.76, 7.32) * mm});
            skArc(sketch, "E18.trimOffspring", {"start": v(11.72, 5.66) * mm, "mid": v(11.67, 5.76) * mm, "end": v(11.62, 5.85) * mm});
            skArc(sketch, "E19.trimOffspring", {"start": v(12.36, 4.08) * mm, "mid": v(12.32, 4.18) * mm, "end": v(12.29, 4.29) * mm});
            skArc(sketch, "E20.trimOffspring", {"start": v(12.79, 2.43) * mm, "mid": v(12.76, 2.54) * mm, "end": v(12.74, 2.64) * mm});
            skArc(sketch, "E21.trimOffspring", {"start": v(13, 0.74) * mm, "mid": v(12.99, 0.85) * mm, "end": v(12.98, 0.96) * mm});
            skArc(sketch, "E22.trimOffspring", {"start": v(12.98, -0.96) * mm, "mid": v(12.99, -0.85) * mm, "end": v(13, -0.74) * mm});
            skArc(sketch, "E23.trimOffspring", {"start": v(12.74, -2.64) * mm, "mid": v(12.76, -2.54) * mm, "end": v(12.79, -2.43) * mm});
            skArc(sketch, "E24.trimOffspring", {"start": v(12.29, -4.29) * mm, "mid": v(12.32, -4.18) * mm, "end": v(12.36, -4.08) * mm});
            skArc(sketch, "E25.trimOffspring", {"start": v(11.62, -5.85) * mm, "mid": v(11.67, -5.76) * mm, "end": v(11.72, -5.66) * mm});
            skArc(sketch, "E26.trimOffspring", {"start": v(10.76, -7.32) * mm, "mid": v(10.82, -7.23) * mm, "end": v(10.88, -7.14) * mm});
            skArc(sketch, "E27.trimOffspring", {"start": v(9.71, -8.66) * mm, "mid": v(9.79, -8.58) * mm, "end": v(9.86, -8.5) * mm});
            skArc(sketch, "E28.trimOffspring", {"start": v(8.5, -9.86) * mm, "mid": v(8.58, -9.79) * mm, "end": v(8.66, -9.71) * mm});
            skArc(sketch, "E29.trimOffspring", {"start": v(7.14, -10.88) * mm, "mid": v(7.23, -10.82) * mm, "end": v(7.32, -10.76) * mm});
            skArc(sketch, "E30.trimOffspring", {"start": v(5.66, -11.72) * mm, "mid": v(5.76, -11.67) * mm, "end": v(5.85, -11.62) * mm});
            skArc(sketch, "E31.trimOffspring", {"start": v(4.08, -12.36) * mm, "mid": v(4.18, -12.32) * mm, "end": v(4.29, -12.29) * mm});
            skArc(sketch, "E32.trimOffspring", {"start": v(2.43, -12.79) * mm, "mid": v(2.54, -12.76) * mm, "end": v(2.64, -12.74) * mm});
            skArc(sketch, "E33.trimOffspring", {"start": v(0.74, -13) * mm, "mid": v(0.85, -12.99) * mm, "end": v(0.96, -12.98) * mm});
            skArc(sketch, "E34.trimOffspring", {"start": v(-0.96, -12.98) * mm, "mid": v(-0.85, -12.99) * mm, "end": v(-0.74, -13) * mm});
            skArc(sketch, "E35.trimOffspring", {"start": v(-2.64, -12.74) * mm, "mid": v(-2.54, -12.76) * mm, "end": v(-2.43, -12.79) * mm});
            skArc(sketch, "E36.trimOffspring", {"start": v(-4.29, -12.29) * mm, "mid": v(-4.18, -12.32) * mm, "end": v(-4.08, -12.36) * mm});
            skArc(sketch, "E37.trimOffspring", {"start": v(-7.32, -10.76) * mm, "mid": v(-6.5, -11.27) * mm, "end": v(-5.66, -11.72) * mm});
            skArc(sketch, "E38.trimOffspring", {"start": v(-8.66, -9.71) * mm, "mid": v(-8.58, -9.79) * mm, "end": v(-8.5, -9.86) * mm});
            skArc(sketch, "E39.trimOffspring", {"start": v(-9.86, -8.5) * mm, "mid": v(-9.79, -8.58) * mm, "end": v(-9.71, -8.66) * mm});
            skArc(sketch, "E40.trimOffspring", {"start": v(-10.88, -7.14) * mm, "mid": v(-10.82, -7.23) * mm, "end": v(-10.76, -7.32) * mm});
            skArc(sketch, "E41.trimOffspring", {"start": v(-11.72, -5.66) * mm, "mid": v(-11.67, -5.76) * mm, "end": v(-11.62, -5.85) * mm});
            skArc(sketch, "E42.trimOffspring", {"start": v(-12.36, -4.08) * mm, "mid": v(-12.32, -4.18) * mm, "end": v(-12.29, -4.29) * mm});
            skArc(sketch, "E43.trimOffspring", {"start": v(-12.79, -2.43) * mm, "mid": v(-12.76, -2.54) * mm, "end": v(-12.74, -2.64) * mm});
            skArc(sketch, "E44.trimOffspring", {"start": v(-13, -0.74) * mm, "mid": v(-12.99, -0.85) * mm, "end": v(-12.98, -0.96) * mm});
            skArc(sketch, "E45.trimOffspring", {"start": v(-12.98, 0.96) * mm, "mid": v(-12.99, 0.85) * mm, "end": v(-13, 0.74) * mm});
            skArc(sketch, "E46.trimOffspring", {"start": v(-12.74, 2.64) * mm, "mid": v(-12.76, 2.54) * mm, "end": v(-12.79, 2.43) * mm});
            skArc(sketch, "E47.trimOffspring", {"start": v(-12.29, 4.29) * mm, "mid": v(-12.32, 4.18) * mm, "end": v(-12.36, 4.08) * mm});
            skArc(sketch, "E48.trimOffspring", {"start": v(-11.62, 5.85) * mm, "mid": v(-11.67, 5.76) * mm, "end": v(-11.72, 5.66) * mm});
            skArc(sketch, "E49.trimOffspring", {"start": v(-10.76, 7.32) * mm, "mid": v(-10.82, 7.23) * mm, "end": v(-10.88, 7.14) * mm});
            skArc(sketch, "E50.trimOffspring", {"start": v(-9.71, 8.66) * mm, "mid": v(-9.79, 8.58) * mm, "end": v(-9.86, 8.5) * mm});
            skArc(sketch, "E51.trimOffspring", {"start": v(-8.5, 9.86) * mm, "mid": v(-8.58, 9.79) * mm, "end": v(-8.66, 9.71) * mm});
            skArc(sketch, "E52.trimOffspring", {"start": v(-7.14, 10.88) * mm, "mid": v(-7.23, 10.82) * mm, "end": v(-7.32, 10.76) * mm});
            skArc(sketch, "E53.trimOffspring", {"start": v(-5.66, 11.72) * mm, "mid": v(-5.76, 11.67) * mm, "end": v(-5.85, 11.62) * mm});
            skArc(sketch, "E54.trimOffspring", {"start": v(-4.08, 12.36) * mm, "mid": v(-4.18, 12.32) * mm, "end": v(-4.29, 12.29) * mm});
            skArc(sketch, "E55.trimOffspring", {"start": v(-2.43, 12.79) * mm, "mid": v(-2.54, 12.76) * mm, "end": v(-2.64, 12.74) * mm});
            skSolve(sketch);
        }
        {
            var Q0;
            {var subQ0=sQuery(id+"F0.wireOp",EDGE,"E1");var subQ38=makeQuery(id+"F0.imprint","IMPRINT",VERTEX,{"derivedFrom":subQ0});Q0=makeQuery(id+"F0.imprint","IMPRINT",FACE,{"disambiguationData":[TD([[makeQuery(id+"F0.imprint","IMPRINT",EDGE,{"disambiguationData":[TD([[subQ38,1.0]])],"derivedFrom":subQ0}),1.0]])]});}
            var Q1;
            Q1=makeQuery(id+"F0.imprint","IMPRINT",FACE,{"disambiguationData":[TD([[makeQuery(id+"F0.imprint","IMPRINT",EDGE,{"derivedFrom":sQuery(id+"F0.wireOp",EDGE,"E9.4.0")}),1.0]])]});
            var Q2;
            Q2=makeQuery(id+"F0.imprint","IMPRINT",FACE,{"disambiguationData":[TD([[makeQuery(id+"F0.imprint","IMPRINT",EDGE,{"derivedFrom":sQuery(id+"F0.wireOp",EDGE,"E9.3.0")}),1.0]])]});
            var Q3;
            Q3=makeQuery(id+"F0.imprint","IMPRINT",FACE,{"disambiguationData":[TD([[makeQuery(id+"F0.imprint","IMPRINT",EDGE,{"derivedFrom":sQuery(id+"F0.wireOp",EDGE,"E9.2.0")}),1.0]])]});
            var Q4;
            Q4=makeQuery(id+"F0.imprint","IMPRINT",FACE,{"disambiguationData":[TD([[makeQuery(id+"F0.imprint","IMPRINT",EDGE,{"derivedFrom":sQuery(id+"F0.wireOp",EDGE,"E9.1.0")}),1.0]])]});
            var Q5;
            Q5=makeQuery(id+"F0.imprint","IMPRINT",FACE,{"disambiguationData":[TD([[makeQuery(id+"F0.imprint","IMPRINT",EDGE,{"derivedFrom":sQuery(id+"F0.wireOp",EDGE,"E0")}),1.0]])]});
            var Q6;
            Q6=makeQuery(id+"F0.imprint","IMPRINT",FACE,{"disambiguationData":[TD([[makeQuery(id+"F0.imprint","IMPRINT",EDGE,{"derivedFrom":sQuery(id+"F0.wireOp",EDGE,"E6.MirrorCS")}),-1.0]])]});
            var Q7;
            Q7=makeQuery(id+"F0.imprint","IMPRINT",FACE,{"disambiguationData":[TD([[makeQuery(id+"F0.imprint","IMPRINT",EDGE,{"derivedFrom":sQuery(id+"F0.wireOp",EDGE,"E9.46.0")}),1.0]])]});
            var Q8;
            Q8=makeQuery(id+"F0.imprint","IMPRINT",FACE,{"disambiguationData":[TD([[makeQuery(id+"F0.imprint","IMPRINT",EDGE,{"derivedFrom":sQuery(id+"F0.wireOp",EDGE,"E9.45.0")}),1.0]])]});
            var Q9;
            Q9=makeQuery(id+"F0.imprint","IMPRINT",FACE,{"disambiguationData":[TD([[makeQuery(id+"F0.imprint","IMPRINT",EDGE,{"derivedFrom":sQuery(id+"F0.wireOp",EDGE,"E9.44.0")}),1.0]])]});
            var Q10;
            Q10=makeQuery(id+"F0.imprint","IMPRINT",FACE,{"disambiguationData":[TD([[makeQuery(id+"F0.imprint","IMPRINT",EDGE,{"derivedFrom":sQuery(id+"F0.wireOp",EDGE,"E9.43.0")}),1.0]])]});
            var Q11;
            Q11=makeQuery(id+"F0.imprint","IMPRINT",FACE,{"disambiguationData":[TD([[makeQuery(id+"F0.imprint","IMPRINT",EDGE,{"derivedFrom":sQuery(id+"F0.wireOp",EDGE,"E9.42.0")}),1.0]])]});
            var Q12;
            Q12=makeQuery(id+"F0.imprint","IMPRINT",FACE,{"disambiguationData":[TD([[makeQuery(id+"F0.imprint","IMPRINT",EDGE,{"derivedFrom":sQuery(id+"F0.wireOp",EDGE,"E9.41.0")}),1.0]])]});
            var Q13;
            Q13=makeQuery(id+"F0.imprint","IMPRINT",FACE,{"disambiguationData":[TD([[makeQuery(id+"F0.imprint","IMPRINT",EDGE,{"derivedFrom":sQuery(id+"F0.wireOp",EDGE,"E9.40.0")}),1.0]])]});
            var Q14;
            Q14=makeQuery(id+"F0.imprint","IMPRINT",FACE,{"disambiguationData":[TD([[makeQuery(id+"F0.imprint","IMPRINT",EDGE,{"derivedFrom":sQuery(id+"F0.wireOp",EDGE,"E9.39.0")}),1.0]])]});
            var Q15;
            Q15=makeQuery(id+"F0.imprint","IMPRINT",FACE,{"disambiguationData":[TD([[makeQuery(id+"F0.imprint","IMPRINT",EDGE,{"derivedFrom":sQuery(id+"F0.wireOp",EDGE,"E9.38.0")}),1.0]])]});
            var Q16;
            Q16=makeQuery(id+"F0.imprint","IMPRINT",FACE,{"disambiguationData":[TD([[makeQuery(id+"F0.imprint","IMPRINT",EDGE,{"derivedFrom":sQuery(id+"F0.wireOp",EDGE,"E9.37.0")}),1.0]])]});
            var Q17;
            Q17=makeQuery(id+"F0.imprint","IMPRINT",FACE,{"disambiguationData":[TD([[makeQuery(id+"F0.imprint","IMPRINT",EDGE,{"derivedFrom":sQuery(id+"F0.wireOp",EDGE,"E9.36.0")}),1.0]])]});
            var Q18;
            Q18=makeQuery(id+"F0.imprint","IMPRINT",FACE,{"disambiguationData":[TD([[makeQuery(id+"F0.imprint","IMPRINT",EDGE,{"derivedFrom":sQuery(id+"F0.wireOp",EDGE,"E9.35.0")}),1.0]])]});
            var Q19;
            Q19=makeQuery(id+"F0.imprint","IMPRINT",FACE,{"disambiguationData":[TD([[makeQuery(id+"F0.imprint","IMPRINT",EDGE,{"derivedFrom":sQuery(id+"F0.wireOp",EDGE,"E9.34.0")}),1.0]])]});
            var Q20;
            Q20=makeQuery(id+"F0.imprint","IMPRINT",FACE,{"disambiguationData":[TD([[makeQuery(id+"F0.imprint","IMPRINT",EDGE,{"derivedFrom":sQuery(id+"F0.wireOp",EDGE,"E9.33.0")}),1.0]])]});
            var Q21;
            Q21=makeQuery(id+"F0.imprint","IMPRINT",FACE,{"disambiguationData":[TD([[makeQuery(id+"F0.imprint","IMPRINT",EDGE,{"derivedFrom":sQuery(id+"F0.wireOp",EDGE,"E9.32.0")}),1.0]])]});
            var Q22;
            Q22=makeQuery(id+"F0.imprint","IMPRINT",FACE,{"disambiguationData":[TD([[makeQuery(id+"F0.imprint","IMPRINT",EDGE,{"derivedFrom":sQuery(id+"F0.wireOp",EDGE,"E9.31.0")}),1.0]])]});
            var Q23;
            Q23=makeQuery(id+"F0.imprint","IMPRINT",FACE,{"disambiguationData":[TD([[makeQuery(id+"F0.imprint","IMPRINT",EDGE,{"derivedFrom":sQuery(id+"F0.wireOp",EDGE,"E9.30.0")}),1.0]])]});
            var Q24;
            Q24=makeQuery(id+"F0.imprint","IMPRINT",FACE,{"disambiguationData":[TD([[makeQuery(id+"F0.imprint","IMPRINT",EDGE,{"derivedFrom":sQuery(id+"F0.wireOp",EDGE,"E9.29.0")}),1.0]])]});
            var Q25;
            Q25=makeQuery(id+"F0.imprint","IMPRINT",FACE,{"disambiguationData":[TD([[makeQuery(id+"F0.imprint","IMPRINT",EDGE,{"derivedFrom":sQuery(id+"F0.wireOp",EDGE,"E9.28.0")}),1.0]])]});
            var Q26;
            Q26=makeQuery(id+"F0.imprint","IMPRINT",FACE,{"disambiguationData":[TD([[makeQuery(id+"F0.imprint","IMPRINT",EDGE,{"derivedFrom":sQuery(id+"F0.wireOp",EDGE,"E9.27.0")}),1.0]])]});
            var Q27;
            Q27=makeQuery(id+"F0.imprint","IMPRINT",FACE,{"disambiguationData":[TD([[makeQuery(id+"F0.imprint","IMPRINT",EDGE,{"derivedFrom":sQuery(id+"F0.wireOp",EDGE,"E9.26.0")}),1.0]])]});
            var Q28;
            Q28=makeQuery(id+"F0.imprint","IMPRINT",FACE,{"disambiguationData":[TD([[makeQuery(id+"F0.imprint","IMPRINT",EDGE,{"derivedFrom":sQuery(id+"F0.wireOp",EDGE,"E9.25.0")}),1.0]])]});
            var Q29;
            Q29=makeQuery(id+"F0.imprint","IMPRINT",FACE,{"disambiguationData":[TD([[makeQuery(id+"F0.imprint","IMPRINT",EDGE,{"derivedFrom":sQuery(id+"F0.wireOp",EDGE,"E9.24.0")}),1.0]])]});
            var Q30;
            Q30=makeQuery(id+"F0.imprint","IMPRINT",FACE,{"disambiguationData":[TD([[makeQuery(id+"F0.imprint","IMPRINT",EDGE,{"derivedFrom":sQuery(id+"F0.wireOp",EDGE,"E9.23.0")}),1.0]])]});
            var Q31;
            Q31=makeQuery(id+"F0.imprint","IMPRINT",FACE,{"disambiguationData":[TD([[makeQuery(id+"F0.imprint","IMPRINT",EDGE,{"derivedFrom":sQuery(id+"F0.wireOp",EDGE,"E9.22.0")}),1.0]])]});
            var Q32;
            Q32=makeQuery(id+"F0.imprint","IMPRINT",FACE,{"disambiguationData":[TD([[makeQuery(id+"F0.imprint","IMPRINT",EDGE,{"derivedFrom":sQuery(id+"F0.wireOp",EDGE,"E9.21.0")}),1.0]])]});
            var Q33;
            {var subQ1=sQuery(id+"F0.wireOp",EDGE,"E9.20.0");Q33=makeQuery(id+"F0.imprint","IMPRINT",FACE,{"disambiguationData":[TD([[makeQuery(id+"F0.imprint","IMPRINT",EDGE,{"derivedFrom":subQ1}),1.0]])]});}
            var Q34;
            {var subQ3=sQuery(id+"F0.wireOp",EDGE,"E9.19.0");Q34=makeQuery(id+"F0.imprint","IMPRINT",FACE,{"disambiguationData":[TD([[makeQuery(id+"F0.imprint","IMPRINT",EDGE,{"derivedFrom":subQ3}),1.0]])]});}
            var Q35;
            Q35=makeQuery(id+"F0.imprint","IMPRINT",FACE,{"disambiguationData":[TD([[makeQuery(id+"F0.imprint","IMPRINT",EDGE,{"derivedFrom":sQuery(id+"F0.wireOp",EDGE,"E9.18.0")}),1.0]])]});
            var Q36;
            Q36=makeQuery(id+"F0.imprint","IMPRINT",FACE,{"disambiguationData":[TD([[makeQuery(id+"F0.imprint","IMPRINT",EDGE,{"derivedFrom":sQuery(id+"F0.wireOp",EDGE,"E9.17.0")}),1.0]])]});
            var Q37;
            Q37=makeQuery(id+"F0.imprint","IMPRINT",FACE,{"disambiguationData":[TD([[makeQuery(id+"F0.imprint","IMPRINT",EDGE,{"derivedFrom":sQuery(id+"F0.wireOp",EDGE,"E9.16.0")}),1.0]])]});
            var Q38;
            Q38=makeQuery(id+"F0.imprint","IMPRINT",FACE,{"disambiguationData":[TD([[makeQuery(id+"F0.imprint","IMPRINT",EDGE,{"derivedFrom":sQuery(id+"F0.wireOp",EDGE,"E9.15.0")}),1.0]])]});
            var Q39;
            Q39=makeQuery(id+"F0.imprint","IMPRINT",FACE,{"disambiguationData":[TD([[makeQuery(id+"F0.imprint","IMPRINT",EDGE,{"derivedFrom":sQuery(id+"F0.wireOp",EDGE,"E9.14.0")}),1.0]])]});
            var Q40;
            Q40=makeQuery(id+"F0.imprint","IMPRINT",FACE,{"disambiguationData":[TD([[makeQuery(id+"F0.imprint","IMPRINT",EDGE,{"derivedFrom":sQuery(id+"F0.wireOp",EDGE,"E9.13.0")}),1.0]])]});
            var Q41;
            Q41=makeQuery(id+"F0.imprint","IMPRINT",FACE,{"disambiguationData":[TD([[makeQuery(id+"F0.imprint","IMPRINT",EDGE,{"derivedFrom":sQuery(id+"F0.wireOp",EDGE,"E9.12.0")}),1.0]])]});
            var Q42;
            Q42=makeQuery(id+"F0.imprint","IMPRINT",FACE,{"disambiguationData":[TD([[makeQuery(id+"F0.imprint","IMPRINT",EDGE,{"derivedFrom":sQuery(id+"F0.wireOp",EDGE,"E9.11.0")}),1.0]])]});
            var Q43;
            Q43=makeQuery(id+"F0.imprint","IMPRINT",FACE,{"disambiguationData":[TD([[makeQuery(id+"F0.imprint","IMPRINT",EDGE,{"derivedFrom":sQuery(id+"F0.wireOp",EDGE,"E9.10.0")}),1.0]])]});
            var Q44;
            Q44=makeQuery(id+"F0.imprint","IMPRINT",FACE,{"disambiguationData":[TD([[makeQuery(id+"F0.imprint","IMPRINT",EDGE,{"derivedFrom":sQuery(id+"F0.wireOp",EDGE,"E9.7.0")}),1.0]])]});
            var Q45;
            Q45=makeQuery(id+"F0.imprint","IMPRINT",FACE,{"disambiguationData":[TD([[makeQuery(id+"F0.imprint","IMPRINT",EDGE,{"derivedFrom":sQuery(id+"F0.wireOp",EDGE,"E9.6.0")}),1.0]])]});
            var Q46;
            Q46=makeQuery(id+"F0.imprint","IMPRINT",FACE,{"disambiguationData":[TD([[makeQuery(id+"F0.imprint","IMPRINT",EDGE,{"derivedFrom":sQuery(id+"F0.wireOp",EDGE,"E9.5.0")}),1.0]])]});
            var Q47;
            Q47=makeQuery(id+"F0.imprint","IMPRINT",FACE,{"disambiguationData":[TD([[makeQuery(id+"F0.imprint","IMPRINT",EDGE,{"derivedFrom":sQuery(id+"F0.wireOp",EDGE,"E9.8.0")}),1.0]])]});
            var Q48;
            Q48=makeQuery(id+"F0.imprint","IMPRINT",FACE,{"disambiguationData":[TD([[makeQuery(id+"F0.imprint","IMPRINT",EDGE,{"derivedFrom":sQuery(id+"F0.wireOp",EDGE,"E9.9.0")}),1.0]])]});
            extrude(context, id + "F1", {"entities" : qUnion([Q0, Q1, Q2, Q3, Q4, Q5, Q6, Q7, Q8, Q9, Q10, Q11, Q12, Q13, Q14, Q15, Q16, Q17, Q18, Q19, Q20, Q21, Q22, Q23, Q24, Q25, Q26, Q27, Q28, Q29, Q30, Q31, Q32, Q33, Q34, Q35, Q36, Q37, Q38, Q39, Q40, Q41, Q42, Q43, Q44, Q45, Q46, Q47, Q48]), "depth" : 6.5 * mm, "offsetDistance" : 25 * mm});
        }
        {
            var Q0;
            Q0=makeQuery(id+"F1.opExtrude","CAP_FACE",FACE,{"disambiguationData":[OSD([sQuery(id+"F0.wireOp",EDGE,"E0"),sQuery(id+"F0.wireOp",EDGE,"E2"),sQuery(id+"F0.wireOp",EDGE,"E4"),sQuery(id+"F0.wireOp",EDGE,"E5"),sQuery(id+"F0.wireOp",EDGE,"E6.MirrorCS"),sQuery(id+"F0.wireOp",EDGE,"E7.MirrorCS"),sQuery(id+"F0.wireOp",EDGE,"E8.MirrorCS"),sQuery(id+"F0.wireOp",EDGE,"E9.1.0"),sQuery(id+"F0.wireOp",EDGE,"E9.1.1"),sQuery(id+"F0.wireOp",EDGE,"E9.1.2"),sQuery(id+"F0.wireOp",EDGE,"E9.1.3"),sQuery(id+"F0.wireOp",EDGE,"E9.1.4"),sQuery(id+"F0.wireOp",EDGE,"E9.1.5"),sQuery(id+"F0.wireOp",EDGE,"E9.2.0"),sQuery(id+"F0.wireOp",EDGE,"E9.2.1"),sQuery(id+"F0.wireOp",EDGE,"E9.2.2"),sQuery(id+"F0.wireOp",EDGE,"E9.2.3"),sQuery(id+"F0.wireOp",EDGE,"E9.2.4"),sQuery(id+"F0.wireOp",EDGE,"E9.2.5"),sQuery(id+"F0.wireOp",EDGE,"E9.3.0"),sQuery(id+"F0.wireOp",EDGE,"E9.3.1"),sQuery(id+"F0.wireOp",EDGE,"E9.3.2"),sQuery(id+"F0.wireOp",EDGE,"E9.3.3"),sQuery(id+"F0.wireOp",EDGE,"E9.3.4"),sQuery(id+"F0.wireOp",EDGE,"E9.3.5"),sQuery(id+"F0.wireOp",EDGE,"E9.4.0"),sQuery(id+"F0.wireOp",EDGE,"E9.4.1"),sQuery(id+"F0.wireOp",EDGE,"E9.4.2"),sQuery(id+"F0.wireOp",EDGE,"E9.4.3"),sQuery(id+"F0.wireOp",EDGE,"E9.4.4"),sQuery(id+"F0.wireOp",EDGE,"E9.4.5"),sQuery(id+"F0.wireOp",EDGE,"E9.5.0"),sQuery(id+"F0.wireOp",EDGE,"E9.5.1"),sQuery(id+"F0.wireOp",EDGE,"E9.5.2"),sQuery(id+"F0.wireOp",EDGE,"E9.5.3"),sQuery(id+"F0.wireOp",EDGE,"E9.5.4"),sQuery(id+"F0.wireOp",EDGE,"E9.5.5"),sQuery(id+"F0.wireOp",EDGE,"E9.6.0"),sQuery(id+"F0.wireOp",EDGE,"E9.6.1"),sQuery(id+"F0.wireOp",EDGE,"E9.6.2"),sQuery(id+"F0.wireOp",EDGE,"E9.6.3"),sQuery(id+"F0.wireOp",EDGE,"E9.6.4"),sQuery(id+"F0.wireOp",EDGE,"E9.6.5"),sQuery(id+"F0.wireOp",EDGE,"E9.7.0"),sQuery(id+"F0.wireOp",EDGE,"E9.7.1"),sQuery(id+"F0.wireOp",EDGE,"E9.7.2"),sQuery(id+"F0.wireOp",EDGE,"E9.7.3"),sQuery(id+"F0.wireOp",EDGE,"E9.7.4"),sQuery(id+"F0.wireOp",EDGE,"E9.7.5"),sQuery(id+"F0.wireOp",EDGE,"E9.8.0"),sQuery(id+"F0.wireOp",EDGE,"E9.8.1"),sQuery(id+"F0.wireOp",EDGE,"E9.8.2"),sQuery(id+"F0.wireOp",EDGE,"E9.8.3"),sQuery(id+"F0.wireOp",EDGE,"E9.8.4"),sQuery(id+"F0.wireOp",EDGE,"E9.8.5"),sQuery(id+"F0.wireOp",EDGE,"E9.9.0"),sQuery(id+"F0.wireOp",EDGE,"E9.9.1"),sQuery(id+"F0.wireOp",EDGE,"E9.9.2"),sQuery(id+"F0.wireOp",EDGE,"E9.9.3"),sQuery(id+"F0.wireOp",EDGE,"E9.9.4"),sQuery(id+"F0.wireOp",EDGE,"E9.9.5"),sQuery(id+"F0.wireOp",EDGE,"E9.10.0"),sQuery(id+"F0.wireOp",EDGE,"E9.10.1"),sQuery(id+"F0.wireOp",EDGE,"E9.10.2"),sQuery(id+"F0.wireOp",EDGE,"E9.10.3"),sQuery(id+"F0.wireOp",EDGE,"E9.10.4"),sQuery(id+"F0.wireOp",EDGE,"E9.10.5"),sQuery(id+"F0.wireOp",EDGE,"E9.11.0"),sQuery(id+"F0.wireOp",EDGE,"E9.11.1"),sQuery(id+"F0.wireOp",EDGE,"E9.11.2"),sQuery(id+"F0.wireOp",EDGE,"E9.11.3"),sQuery(id+"F0.wireOp",EDGE,"E9.11.4"),sQuery(id+"F0.wireOp",EDGE,"E9.11.5"),sQuery(id+"F0.wireOp",EDGE,"E9.12.0"),sQuery(id+"F0.wireOp",EDGE,"E9.12.1"),sQuery(id+"F0.wireOp",EDGE,"E9.12.2"),sQuery(id+"F0.wireOp",EDGE,"E9.12.3"),sQuery(id+"F0.wireOp",EDGE,"E9.12.4"),sQuery(id+"F0.wireOp",EDGE,"E9.12.5"),sQuery(id+"F0.wireOp",EDGE,"E9.13.0"),sQuery(id+"F0.wireOp",EDGE,"E9.13.1"),sQuery(id+"F0.wireOp",EDGE,"E9.13.2"),sQuery(id+"F0.wireOp",EDGE,"E9.13.3"),sQuery(id+"F0.wireOp",EDGE,"E9.13.4"),sQuery(id+"F0.wireOp",EDGE,"E9.13.5"),sQuery(id+"F0.wireOp",EDGE,"E9.14.0"),sQuery(id+"F0.wireOp",EDGE,"E9.14.1"),sQuery(id+"F0.wireOp",EDGE,"E9.14.2"),sQuery(id+"F0.wireOp",EDGE,"E9.14.3"),sQuery(id+"F0.wireOp",EDGE,"E9.14.4"),sQuery(id+"F0.wireOp",EDGE,"E9.14.5"),sQuery(id+"F0.wireOp",EDGE,"E9.15.0"),sQuery(id+"F0.wireOp",EDGE,"E9.15.1"),sQuery(id+"F0.wireOp",EDGE,"E9.15.2"),sQuery(id+"F0.wireOp",EDGE,"E9.15.3"),sQuery(id+"F0.wireOp",EDGE,"E9.15.4"),sQuery(id+"F0.wireOp",EDGE,"E9.15.5"),sQuery(id+"F0.wireOp",EDGE,"E9.16.0"),sQuery(id+"F0.wireOp",EDGE,"E9.16.1"),sQuery(id+"F0.wireOp",EDGE,"E9.16.2"),sQuery(id+"F0.wireOp",EDGE,"E9.16.3"),sQuery(id+"F0.wireOp",EDGE,"E9.16.4"),sQuery(id+"F0.wireOp",EDGE,"E9.16.5"),sQuery(id+"F0.wireOp",EDGE,"E9.17.0"),sQuery(id+"F0.wireOp",EDGE,"E9.17.1"),sQuery(id+"F0.wireOp",EDGE,"E9.17.2"),sQuery(id+"F0.wireOp",EDGE,"E9.17.3"),sQuery(id+"F0.wireOp",EDGE,"E9.17.4"),sQuery(id+"F0.wireOp",EDGE,"E9.17.5"),sQuery(id+"F0.wireOp",EDGE,"E9.18.0"),sQuery(id+"F0.wireOp",EDGE,"E9.18.1"),sQuery(id+"F0.wireOp",EDGE,"E9.18.2"),sQuery(id+"F0.wireOp",EDGE,"E9.18.3"),sQuery(id+"F0.wireOp",EDGE,"E9.18.4"),sQuery(id+"F0.wireOp",EDGE,"E9.18.5"),sQuery(id+"F0.wireOp",EDGE,"E9.19.0"),sQuery(id+"F0.wireOp",EDGE,"E9.19.1"),sQuery(id+"F0.wireOp",EDGE,"E9.19.2"),sQuery(id+"F0.wireOp",EDGE,"E9.19.3"),sQuery(id+"F0.wireOp",EDGE,"E9.19.4"),sQuery(id+"F0.wireOp",EDGE,"E9.19.5"),sQuery(id+"F0.wireOp",EDGE,"E9.20.0"),sQuery(id+"F0.wireOp",EDGE,"E9.20.1"),sQuery(id+"F0.wireOp",EDGE,"E9.20.2"),sQuery(id+"F0.wireOp",EDGE,"E9.20.3"),sQuery(id+"F0.wireOp",EDGE,"E9.20.4"),sQuery(id+"F0.wireOp",EDGE,"E9.20.5"),sQuery(id+"F0.wireOp",EDGE,"E9.21.0"),sQuery(id+"F0.wireOp",EDGE,"E9.21.1"),sQuery(id+"F0.wireOp",EDGE,"E9.21.2"),sQuery(id+"F0.wireOp",EDGE,"E9.21.3"),sQuery(id+"F0.wireOp",EDGE,"E9.21.4"),sQuery(id+"F0.wireOp",EDGE,"E9.21.5"),sQuery(id+"F0.wireOp",EDGE,"E9.22.0"),sQuery(id+"F0.wireOp",EDGE,"E9.22.1"),sQuery(id+"F0.wireOp",EDGE,"E9.22.2"),sQuery(id+"F0.wireOp",EDGE,"E9.22.3"),sQuery(id+"F0.wireOp",EDGE,"E9.22.4"),sQuery(id+"F0.wireOp",EDGE,"E9.22.5"),sQuery(id+"F0.wireOp",EDGE,"E9.23.0"),sQuery(id+"F0.wireOp",EDGE,"E9.23.1"),sQuery(id+"F0.wireOp",EDGE,"E9.23.2"),sQuery(id+"F0.wireOp",EDGE,"E9.23.3"),sQuery(id+"F0.wireOp",EDGE,"E9.23.4"),sQuery(id+"F0.wireOp",EDGE,"E9.23.5"),sQuery(id+"F0.wireOp",EDGE,"E9.24.0"),sQuery(id+"F0.wireOp",EDGE,"E9.24.1"),sQuery(id+"F0.wireOp",EDGE,"E9.24.2"),sQuery(id+"F0.wireOp",EDGE,"E9.24.3"),sQuery(id+"F0.wireOp",EDGE,"E9.24.4"),sQuery(id+"F0.wireOp",EDGE,"E9.24.5"),sQuery(id+"F0.wireOp",EDGE,"E9.25.0"),sQuery(id+"F0.wireOp",EDGE,"E9.25.1"),sQuery(id+"F0.wireOp",EDGE,"E9.25.2"),sQuery(id+"F0.wireOp",EDGE,"E9.25.3"),sQuery(id+"F0.wireOp",EDGE,"E9.25.4"),sQuery(id+"F0.wireOp",EDGE,"E9.25.5"),sQuery(id+"F0.wireOp",EDGE,"E9.26.0"),sQuery(id+"F0.wireOp",EDGE,"E9.26.1"),sQuery(id+"F0.wireOp",EDGE,"E9.26.2"),sQuery(id+"F0.wireOp",EDGE,"E9.26.3"),sQuery(id+"F0.wireOp",EDGE,"E9.26.4"),sQuery(id+"F0.wireOp",EDGE,"E9.26.5"),sQuery(id+"F0.wireOp",EDGE,"E9.27.0"),sQuery(id+"F0.wireOp",EDGE,"E9.27.1"),sQuery(id+"F0.wireOp",EDGE,"E9.27.2"),sQuery(id+"F0.wireOp",EDGE,"E9.27.3"),sQuery(id+"F0.wireOp",EDGE,"E9.27.4"),sQuery(id+"F0.wireOp",EDGE,"E9.27.5"),sQuery(id+"F0.wireOp",EDGE,"E9.28.0"),sQuery(id+"F0.wireOp",EDGE,"E9.28.1"),sQuery(id+"F0.wireOp",EDGE,"E9.28.2"),sQuery(id+"F0.wireOp",EDGE,"E9.28.3"),sQuery(id+"F0.wireOp",EDGE,"E9.28.4"),sQuery(id+"F0.wireOp",EDGE,"E9.28.5"),sQuery(id+"F0.wireOp",EDGE,"E9.29.0"),sQuery(id+"F0.wireOp",EDGE,"E9.29.1"),sQuery(id+"F0.wireOp",EDGE,"E9.29.2"),sQuery(id+"F0.wireOp",EDGE,"E9.29.3"),sQuery(id+"F0.wireOp",EDGE,"E9.29.4"),sQuery(id+"F0.wireOp",EDGE,"E9.29.5"),sQuery(id+"F0.wireOp",EDGE,"E9.30.0"),sQuery(id+"F0.wireOp",EDGE,"E9.30.1"),sQuery(id+"F0.wireOp",EDGE,"E9.30.2"),sQuery(id+"F0.wireOp",EDGE,"E9.30.3"),sQuery(id+"F0.wireOp",EDGE,"E9.30.4"),sQuery(id+"F0.wireOp",EDGE,"E9.30.5"),sQuery(id+"F0.wireOp",EDGE,"E9.31.0"),sQuery(id+"F0.wireOp",EDGE,"E9.31.1"),sQuery(id+"F0.wireOp",EDGE,"E9.31.2"),sQuery(id+"F0.wireOp",EDGE,"E9.31.3"),sQuery(id+"F0.wireOp",EDGE,"E9.31.4"),sQuery(id+"F0.wireOp",EDGE,"E9.31.5"),sQuery(id+"F0.wireOp",EDGE,"E9.32.0"),sQuery(id+"F0.wireOp",EDGE,"E9.32.1"),sQuery(id+"F0.wireOp",EDGE,"E9.32.2"),sQuery(id+"F0.wireOp",EDGE,"E9.32.3"),sQuery(id+"F0.wireOp",EDGE,"E9.32.4"),sQuery(id+"F0.wireOp",EDGE,"E9.32.5"),sQuery(id+"F0.wireOp",EDGE,"E9.33.0"),sQuery(id+"F0.wireOp",EDGE,"E9.33.1"),sQuery(id+"F0.wireOp",EDGE,"E9.33.2"),sQuery(id+"F0.wireOp",EDGE,"E9.33.3"),sQuery(id+"F0.wireOp",EDGE,"E9.33.4"),sQuery(id+"F0.wireOp",EDGE,"E9.33.5"),sQuery(id+"F0.wireOp",EDGE,"E9.34.0"),sQuery(id+"F0.wireOp",EDGE,"E9.34.1"),sQuery(id+"F0.wireOp",EDGE,"E9.34.2"),sQuery(id+"F0.wireOp",EDGE,"E9.34.3"),sQuery(id+"F0.wireOp",EDGE,"E9.34.4"),sQuery(id+"F0.wireOp",EDGE,"E9.34.5"),sQuery(id+"F0.wireOp",EDGE,"E9.35.0"),sQuery(id+"F0.wireOp",EDGE,"E9.35.1"),sQuery(id+"F0.wireOp",EDGE,"E9.35.2"),sQuery(id+"F0.wireOp",EDGE,"E9.35.3"),sQuery(id+"F0.wireOp",EDGE,"E9.35.4"),sQuery(id+"F0.wireOp",EDGE,"E9.35.5"),sQuery(id+"F0.wireOp",EDGE,"E9.36.0"),sQuery(id+"F0.wireOp",EDGE,"E9.36.1"),sQuery(id+"F0.wireOp",EDGE,"E9.36.2"),sQuery(id+"F0.wireOp",EDGE,"E9.36.3"),sQuery(id+"F0.wireOp",EDGE,"E9.36.4"),sQuery(id+"F0.wireOp",EDGE,"E9.36.5"),sQuery(id+"F0.wireOp",EDGE,"E9.37.0"),sQuery(id+"F0.wireOp",EDGE,"E9.37.1"),sQuery(id+"F0.wireOp",EDGE,"E9.37.2"),sQuery(id+"F0.wireOp",EDGE,"E9.37.3"),sQuery(id+"F0.wireOp",EDGE,"E9.37.4"),sQuery(id+"F0.wireOp",EDGE,"E9.37.5"),sQuery(id+"F0.wireOp",EDGE,"E9.38.0"),sQuery(id+"F0.wireOp",EDGE,"E9.38.1"),sQuery(id+"F0.wireOp",EDGE,"E9.38.2"),sQuery(id+"F0.wireOp",EDGE,"E9.38.3"),sQuery(id+"F0.wireOp",EDGE,"E9.38.4"),sQuery(id+"F0.wireOp",EDGE,"E9.38.5"),sQuery(id+"F0.wireOp",EDGE,"E9.39.0"),sQuery(id+"F0.wireOp",EDGE,"E9.39.1"),sQuery(id+"F0.wireOp",EDGE,"E9.39.2"),sQuery(id+"F0.wireOp",EDGE,"E9.39.3"),sQuery(id+"F0.wireOp",EDGE,"E9.39.4"),sQuery(id+"F0.wireOp",EDGE,"E9.39.5"),sQuery(id+"F0.wireOp",EDGE,"E9.40.0"),sQuery(id+"F0.wireOp",EDGE,"E9.40.1"),sQuery(id+"F0.wireOp",EDGE,"E9.40.2"),sQuery(id+"F0.wireOp",EDGE,"E9.40.3"),sQuery(id+"F0.wireOp",EDGE,"E9.40.4"),sQuery(id+"F0.wireOp",EDGE,"E9.40.5"),sQuery(id+"F0.wireOp",EDGE,"E9.41.0"),sQuery(id+"F0.wireOp",EDGE,"E9.41.1"),sQuery(id+"F0.wireOp",EDGE,"E9.41.2"),sQuery(id+"F0.wireOp",EDGE,"E9.41.3"),sQuery(id+"F0.wireOp",EDGE,"E9.41.4"),sQuery(id+"F0.wireOp",EDGE,"E9.41.5"),sQuery(id+"F0.wireOp",EDGE,"E9.42.0"),sQuery(id+"F0.wireOp",EDGE,"E9.42.1"),sQuery(id+"F0.wireOp",EDGE,"E9.42.2"),sQuery(id+"F0.wireOp",EDGE,"E9.42.3"),sQuery(id+"F0.wireOp",EDGE,"E9.42.4"),sQuery(id+"F0.wireOp",EDGE,"E9.42.5"),sQuery(id+"F0.wireOp",EDGE,"E9.43.0"),sQuery(id+"F0.wireOp",EDGE,"E9.43.1"),sQuery(id+"F0.wireOp",EDGE,"E9.43.2"),sQuery(id+"F0.wireOp",EDGE,"E9.43.3"),sQuery(id+"F0.wireOp",EDGE,"E9.43.4"),sQuery(id+"F0.wireOp",EDGE,"E9.43.5"),sQuery(id+"F0.wireOp",EDGE,"E9.44.0"),sQuery(id+"F0.wireOp",EDGE,"E9.44.1"),sQuery(id+"F0.wireOp",EDGE,"E9.44.2"),sQuery(id+"F0.wireOp",EDGE,"E9.44.3"),sQuery(id+"F0.wireOp",EDGE,"E9.44.4"),sQuery(id+"F0.wireOp",EDGE,"E9.44.5"),sQuery(id+"F0.wireOp",EDGE,"E9.45.0"),sQuery(id+"F0.wireOp",EDGE,"E9.45.1"),sQuery(id+"F0.wireOp",EDGE,"E9.45.2"),sQuery(id+"F0.wireOp",EDGE,"E9.45.3"),sQuery(id+"F0.wireOp",EDGE,"E9.45.4"),sQuery(id+"F0.wireOp",EDGE,"E9.45.5"),sQuery(id+"F0.wireOp",EDGE,"E9.46.0"),sQuery(id+"F0.wireOp",EDGE,"E9.46.1"),sQuery(id+"F0.wireOp",EDGE,"E9.46.2"),sQuery(id+"F0.wireOp",EDGE,"E9.46.3"),sQuery(id+"F0.wireOp",EDGE,"E9.46.4"),sQuery(id+"F0.wireOp",EDGE,"E9.46.5"),sQuery(id+"F0.wireOp",EDGE,"E9.47.0"),sQuery(id+"F0.wireOp",EDGE,"E9.47.1"),sQuery(id+"F0.wireOp",EDGE,"E9.47.2"),sQuery(id+"F0.wireOp",EDGE,"E9.47.3"),sQuery(id+"F0.wireOp",EDGE,"E9.47.4"),sQuery(id+"F0.wireOp",EDGE,"E9.47.5"),sQuery(id+"F0.wireOp",EDGE,"E10.trimOffspring"),sQuery(id+"F0.wireOp",EDGE,"E11.trimOffspring"),sQuery(id+"F0.wireOp",EDGE,"E12.trimOffspring"),sQuery(id+"F0.wireOp",EDGE,"E13.trimOffspring"),sQuery(id+"F0.wireOp",EDGE,"E14.trimOffspring"),sQuery(id+"F0.wireOp",EDGE,"E15.trimOffspring"),sQuery(id+"F0.wireOp",EDGE,"E16.trimOffspring"),sQuery(id+"F0.wireOp",EDGE,"E17.trimOffspring"),sQuery(id+"F0.wireOp",EDGE,"E18.trimOffspring"),sQuery(id+"F0.wireOp",EDGE,"E19.trimOffspring"),sQuery(id+"F0.wireOp",EDGE,"E20.trimOffspring"),sQuery(id+"F0.wireOp",EDGE,"E21.trimOffspring"),sQuery(id+"F0.wireOp",EDGE,"E22.trimOffspring"),sQuery(id+"F0.wireOp",EDGE,"E23.trimOffspring"),sQuery(id+"F0.wireOp",EDGE,"E24.trimOffspring"),sQuery(id+"F0.wireOp",EDGE,"E25.trimOffspring"),sQuery(id+"F0.wireOp",EDGE,"E26.trimOffspring"),sQuery(id+"F0.wireOp",EDGE,"E27.trimOffspring"),sQuery(id+"F0.wireOp",EDGE,"E28.trimOffspring"),sQuery(id+"F0.wireOp",EDGE,"E29.trimOffspring"),sQuery(id+"F0.wireOp",EDGE,"E30.trimOffspring"),sQuery(id+"F0.wireOp",EDGE,"E31.trimOffspring"),sQuery(id+"F0.wireOp",EDGE,"E32.trimOffspring"),sQuery(id+"F0.wireOp",EDGE,"E33.trimOffspring"),sQuery(id+"F0.wireOp",EDGE,"E34.trimOffspring"),sQuery(id+"F0.wireOp",EDGE,"E35.trimOffspring"),sQuery(id+"F0.wireOp",EDGE,"E36.trimOffspring"),sQuery(id+"F0.wireOp",EDGE,"E37.trimOffspring"),sQuery(id+"F0.wireOp",EDGE,"E38.trimOffspring"),sQuery(id+"F0.wireOp",EDGE,"E39.trimOffspring"),sQuery(id+"F0.wireOp",EDGE,"E40.trimOffspring"),sQuery(id+"F0.wireOp",EDGE,"E41.trimOffspring"),sQuery(id+"F0.wireOp",EDGE,"E42.trimOffspring"),sQuery(id+"F0.wireOp",EDGE,"E43.trimOffspring"),sQuery(id+"F0.wireOp",EDGE,"E44.trimOffspring"),sQuery(id+"F0.wireOp",EDGE,"E45.trimOffspring"),sQuery(id+"F0.wireOp",EDGE,"E46.trimOffspring"),sQuery(id+"F0.wireOp",EDGE,"E47.trimOffspring"),sQuery(id+"F0.wireOp",EDGE,"E48.trimOffspring"),sQuery(id+"F0.wireOp",EDGE,"E49.trimOffspring"),sQuery(id+"F0.wireOp",EDGE,"E50.trimOffspring"),sQuery(id+"F0.wireOp",EDGE,"E51.trimOffspring"),sQuery(id+"F0.wireOp",EDGE,"E52.trimOffspring"),sQuery(id+"F0.wireOp",EDGE,"E53.trimOffspring"),sQuery(id+"F0.wireOp",EDGE,"E54.trimOffspring"),sQuery(id+"F0.wireOp",EDGE,"E55.trimOffspring")])],"isStart":false});
            var sketch = newSketch(context, id + "F2", { "sketchPlane" : qUnion([Q0])});
            skCircle(sketch, "E56", {"center": v(0, 0) * mm, "radius": 14 * mm});
            skSolve(sketch);
        }
        {
            var Q0;
            Q0=makeQuery(id+"F2.imprint","IMPRINT",FACE,{"disambiguationData":[TD([[makeQuery(id+"F2.imprint","IMPRINT",EDGE,{"derivedFrom":sQuery(id+"F2.wireOp",EDGE,"E56")}),1.0]])]});
            var Q1;
            Q1=makeQuery(id+"F2.imprint","IMPRINT",FACE,{"disambiguationData":[TD([[makeQuery(id+"F2.imprint","IMPRINT",EDGE,{"derivedFrom":makeQuery(id+"F1.opExtrude","CAP_EDGE",EDGE,{"disambiguationData":[OSD([sQuery(id+"F0.wireOp",EDGE,"E0")])],"isStart":false})}),1.0]])]});
            extrude(context, id + "F3", {"entities" : qUnion([Q0, Q1]), "operationType" : NewBodyOperationType.ADD, "depth" : .5 * mm, "offsetDistance" : 25 * mm});
        }
        {
            var Q0;
            Q0=makeQuery(id+"F1.opExtrude","CAP_FACE",FACE,{"disambiguationData":[OSD([sQuery(id+"F0.wireOp",EDGE,"E0"),sQuery(id+"F0.wireOp",EDGE,"E2"),sQuery(id+"F0.wireOp",EDGE,"E4"),sQuery(id+"F0.wireOp",EDGE,"E5"),sQuery(id+"F0.wireOp",EDGE,"E6.MirrorCS"),sQuery(id+"F0.wireOp",EDGE,"E7.MirrorCS"),sQuery(id+"F0.wireOp",EDGE,"E8.MirrorCS"),sQuery(id+"F0.wireOp",EDGE,"E9.1.0"),sQuery(id+"F0.wireOp",EDGE,"E9.1.1"),sQuery(id+"F0.wireOp",EDGE,"E9.1.2"),sQuery(id+"F0.wireOp",EDGE,"E9.1.3"),sQuery(id+"F0.wireOp",EDGE,"E9.1.4"),sQuery(id+"F0.wireOp",EDGE,"E9.1.5"),sQuery(id+"F0.wireOp",EDGE,"E9.2.0"),sQuery(id+"F0.wireOp",EDGE,"E9.2.1"),sQuery(id+"F0.wireOp",EDGE,"E9.2.2"),sQuery(id+"F0.wireOp",EDGE,"E9.2.3"),sQuery(id+"F0.wireOp",EDGE,"E9.2.4"),sQuery(id+"F0.wireOp",EDGE,"E9.2.5"),sQuery(id+"F0.wireOp",EDGE,"E9.3.0"),sQuery(id+"F0.wireOp",EDGE,"E9.3.1"),sQuery(id+"F0.wireOp",EDGE,"E9.3.2"),sQuery(id+"F0.wireOp",EDGE,"E9.3.3"),sQuery(id+"F0.wireOp",EDGE,"E9.3.4"),sQuery(id+"F0.wireOp",EDGE,"E9.3.5"),sQuery(id+"F0.wireOp",EDGE,"E9.4.0"),sQuery(id+"F0.wireOp",EDGE,"E9.4.1"),sQuery(id+"F0.wireOp",EDGE,"E9.4.2"),sQuery(id+"F0.wireOp",EDGE,"E9.4.3"),sQuery(id+"F0.wireOp",EDGE,"E9.4.4"),sQuery(id+"F0.wireOp",EDGE,"E9.4.5"),sQuery(id+"F0.wireOp",EDGE,"E9.5.0"),sQuery(id+"F0.wireOp",EDGE,"E9.5.1"),sQuery(id+"F0.wireOp",EDGE,"E9.5.2"),sQuery(id+"F0.wireOp",EDGE,"E9.5.3"),sQuery(id+"F0.wireOp",EDGE,"E9.5.4"),sQuery(id+"F0.wireOp",EDGE,"E9.5.5"),sQuery(id+"F0.wireOp",EDGE,"E9.6.0"),sQuery(id+"F0.wireOp",EDGE,"E9.6.1"),sQuery(id+"F0.wireOp",EDGE,"E9.6.2"),sQuery(id+"F0.wireOp",EDGE,"E9.6.3"),sQuery(id+"F0.wireOp",EDGE,"E9.6.4"),sQuery(id+"F0.wireOp",EDGE,"E9.6.5"),sQuery(id+"F0.wireOp",EDGE,"E9.7.0"),sQuery(id+"F0.wireOp",EDGE,"E9.7.1"),sQuery(id+"F0.wireOp",EDGE,"E9.7.2"),sQuery(id+"F0.wireOp",EDGE,"E9.7.3"),sQuery(id+"F0.wireOp",EDGE,"E9.7.4"),sQuery(id+"F0.wireOp",EDGE,"E9.7.5"),sQuery(id+"F0.wireOp",EDGE,"E9.8.0"),sQuery(id+"F0.wireOp",EDGE,"E9.8.1"),sQuery(id+"F0.wireOp",EDGE,"E9.8.2"),sQuery(id+"F0.wireOp",EDGE,"E9.8.3"),sQuery(id+"F0.wireOp",EDGE,"E9.8.4"),sQuery(id+"F0.wireOp",EDGE,"E9.8.5"),sQuery(id+"F0.wireOp",EDGE,"E9.9.0"),sQuery(id+"F0.wireOp",EDGE,"E9.9.1"),sQuery(id+"F0.wireOp",EDGE,"E9.9.2"),sQuery(id+"F0.wireOp",EDGE,"E9.9.3"),sQuery(id+"F0.wireOp",EDGE,"E9.9.4"),sQuery(id+"F0.wireOp",EDGE,"E9.9.5"),sQuery(id+"F0.wireOp",EDGE,"E9.10.0"),sQuery(id+"F0.wireOp",EDGE,"E9.10.1"),sQuery(id+"F0.wireOp",EDGE,"E9.10.2"),sQuery(id+"F0.wireOp",EDGE,"E9.10.3"),sQuery(id+"F0.wireOp",EDGE,"E9.10.4"),sQuery(id+"F0.wireOp",EDGE,"E9.10.5"),sQuery(id+"F0.wireOp",EDGE,"E9.11.0"),sQuery(id+"F0.wireOp",EDGE,"E9.11.1"),sQuery(id+"F0.wireOp",EDGE,"E9.11.2"),sQuery(id+"F0.wireOp",EDGE,"E9.11.3"),sQuery(id+"F0.wireOp",EDGE,"E9.11.4"),sQuery(id+"F0.wireOp",EDGE,"E9.11.5"),sQuery(id+"F0.wireOp",EDGE,"E9.12.0"),sQuery(id+"F0.wireOp",EDGE,"E9.12.1"),sQuery(id+"F0.wireOp",EDGE,"E9.12.2"),sQuery(id+"F0.wireOp",EDGE,"E9.12.3"),sQuery(id+"F0.wireOp",EDGE,"E9.12.4"),sQuery(id+"F0.wireOp",EDGE,"E9.12.5"),sQuery(id+"F0.wireOp",EDGE,"E9.13.0"),sQuery(id+"F0.wireOp",EDGE,"E9.13.1"),sQuery(id+"F0.wireOp",EDGE,"E9.13.2"),sQuery(id+"F0.wireOp",EDGE,"E9.13.3"),sQuery(id+"F0.wireOp",EDGE,"E9.13.4"),sQuery(id+"F0.wireOp",EDGE,"E9.13.5"),sQuery(id+"F0.wireOp",EDGE,"E9.14.0"),sQuery(id+"F0.wireOp",EDGE,"E9.14.1"),sQuery(id+"F0.wireOp",EDGE,"E9.14.2"),sQuery(id+"F0.wireOp",EDGE,"E9.14.3"),sQuery(id+"F0.wireOp",EDGE,"E9.14.4"),sQuery(id+"F0.wireOp",EDGE,"E9.14.5"),sQuery(id+"F0.wireOp",EDGE,"E9.15.0"),sQuery(id+"F0.wireOp",EDGE,"E9.15.1"),sQuery(id+"F0.wireOp",EDGE,"E9.15.2"),sQuery(id+"F0.wireOp",EDGE,"E9.15.3"),sQuery(id+"F0.wireOp",EDGE,"E9.15.4"),sQuery(id+"F0.wireOp",EDGE,"E9.15.5"),sQuery(id+"F0.wireOp",EDGE,"E9.16.0"),sQuery(id+"F0.wireOp",EDGE,"E9.16.1"),sQuery(id+"F0.wireOp",EDGE,"E9.16.2"),sQuery(id+"F0.wireOp",EDGE,"E9.16.3"),sQuery(id+"F0.wireOp",EDGE,"E9.16.4"),sQuery(id+"F0.wireOp",EDGE,"E9.16.5"),sQuery(id+"F0.wireOp",EDGE,"E9.17.0"),sQuery(id+"F0.wireOp",EDGE,"E9.17.1"),sQuery(id+"F0.wireOp",EDGE,"E9.17.2"),sQuery(id+"F0.wireOp",EDGE,"E9.17.3"),sQuery(id+"F0.wireOp",EDGE,"E9.17.4"),sQuery(id+"F0.wireOp",EDGE,"E9.17.5"),sQuery(id+"F0.wireOp",EDGE,"E9.18.0"),sQuery(id+"F0.wireOp",EDGE,"E9.18.1"),sQuery(id+"F0.wireOp",EDGE,"E9.18.2"),sQuery(id+"F0.wireOp",EDGE,"E9.18.3"),sQuery(id+"F0.wireOp",EDGE,"E9.18.4"),sQuery(id+"F0.wireOp",EDGE,"E9.18.5"),sQuery(id+"F0.wireOp",EDGE,"E9.19.0"),sQuery(id+"F0.wireOp",EDGE,"E9.19.1"),sQuery(id+"F0.wireOp",EDGE,"E9.19.2"),sQuery(id+"F0.wireOp",EDGE,"E9.19.3"),sQuery(id+"F0.wireOp",EDGE,"E9.19.4"),sQuery(id+"F0.wireOp",EDGE,"E9.19.5"),sQuery(id+"F0.wireOp",EDGE,"E9.20.0"),sQuery(id+"F0.wireOp",EDGE,"E9.20.1"),sQuery(id+"F0.wireOp",EDGE,"E9.20.2"),sQuery(id+"F0.wireOp",EDGE,"E9.20.3"),sQuery(id+"F0.wireOp",EDGE,"E9.20.4"),sQuery(id+"F0.wireOp",EDGE,"E9.20.5"),sQuery(id+"F0.wireOp",EDGE,"E9.21.0"),sQuery(id+"F0.wireOp",EDGE,"E9.21.1"),sQuery(id+"F0.wireOp",EDGE,"E9.21.2"),sQuery(id+"F0.wireOp",EDGE,"E9.21.3"),sQuery(id+"F0.wireOp",EDGE,"E9.21.4"),sQuery(id+"F0.wireOp",EDGE,"E9.21.5"),sQuery(id+"F0.wireOp",EDGE,"E9.22.0"),sQuery(id+"F0.wireOp",EDGE,"E9.22.1"),sQuery(id+"F0.wireOp",EDGE,"E9.22.2"),sQuery(id+"F0.wireOp",EDGE,"E9.22.3"),sQuery(id+"F0.wireOp",EDGE,"E9.22.4"),sQuery(id+"F0.wireOp",EDGE,"E9.22.5"),sQuery(id+"F0.wireOp",EDGE,"E9.23.0"),sQuery(id+"F0.wireOp",EDGE,"E9.23.1"),sQuery(id+"F0.wireOp",EDGE,"E9.23.2"),sQuery(id+"F0.wireOp",EDGE,"E9.23.3"),sQuery(id+"F0.wireOp",EDGE,"E9.23.4"),sQuery(id+"F0.wireOp",EDGE,"E9.23.5"),sQuery(id+"F0.wireOp",EDGE,"E9.24.0"),sQuery(id+"F0.wireOp",EDGE,"E9.24.1"),sQuery(id+"F0.wireOp",EDGE,"E9.24.2"),sQuery(id+"F0.wireOp",EDGE,"E9.24.3"),sQuery(id+"F0.wireOp",EDGE,"E9.24.4"),sQuery(id+"F0.wireOp",EDGE,"E9.24.5"),sQuery(id+"F0.wireOp",EDGE,"E9.25.0"),sQuery(id+"F0.wireOp",EDGE,"E9.25.1"),sQuery(id+"F0.wireOp",EDGE,"E9.25.2"),sQuery(id+"F0.wireOp",EDGE,"E9.25.3"),sQuery(id+"F0.wireOp",EDGE,"E9.25.4"),sQuery(id+"F0.wireOp",EDGE,"E9.25.5"),sQuery(id+"F0.wireOp",EDGE,"E9.26.0"),sQuery(id+"F0.wireOp",EDGE,"E9.26.1"),sQuery(id+"F0.wireOp",EDGE,"E9.26.2"),sQuery(id+"F0.wireOp",EDGE,"E9.26.3"),sQuery(id+"F0.wireOp",EDGE,"E9.26.4"),sQuery(id+"F0.wireOp",EDGE,"E9.26.5"),sQuery(id+"F0.wireOp",EDGE,"E9.27.0"),sQuery(id+"F0.wireOp",EDGE,"E9.27.1"),sQuery(id+"F0.wireOp",EDGE,"E9.27.2"),sQuery(id+"F0.wireOp",EDGE,"E9.27.3"),sQuery(id+"F0.wireOp",EDGE,"E9.27.4"),sQuery(id+"F0.wireOp",EDGE,"E9.27.5"),sQuery(id+"F0.wireOp",EDGE,"E9.28.0"),sQuery(id+"F0.wireOp",EDGE,"E9.28.1"),sQuery(id+"F0.wireOp",EDGE,"E9.28.2"),sQuery(id+"F0.wireOp",EDGE,"E9.28.3"),sQuery(id+"F0.wireOp",EDGE,"E9.28.4"),sQuery(id+"F0.wireOp",EDGE,"E9.28.5"),sQuery(id+"F0.wireOp",EDGE,"E9.29.0"),sQuery(id+"F0.wireOp",EDGE,"E9.29.1"),sQuery(id+"F0.wireOp",EDGE,"E9.29.2"),sQuery(id+"F0.wireOp",EDGE,"E9.29.3"),sQuery(id+"F0.wireOp",EDGE,"E9.29.4"),sQuery(id+"F0.wireOp",EDGE,"E9.29.5"),sQuery(id+"F0.wireOp",EDGE,"E9.30.0"),sQuery(id+"F0.wireOp",EDGE,"E9.30.1"),sQuery(id+"F0.wireOp",EDGE,"E9.30.2"),sQuery(id+"F0.wireOp",EDGE,"E9.30.3"),sQuery(id+"F0.wireOp",EDGE,"E9.30.4"),sQuery(id+"F0.wireOp",EDGE,"E9.30.5"),sQuery(id+"F0.wireOp",EDGE,"E9.31.0"),sQuery(id+"F0.wireOp",EDGE,"E9.31.1"),sQuery(id+"F0.wireOp",EDGE,"E9.31.2"),sQuery(id+"F0.wireOp",EDGE,"E9.31.3"),sQuery(id+"F0.wireOp",EDGE,"E9.31.4"),sQuery(id+"F0.wireOp",EDGE,"E9.31.5"),sQuery(id+"F0.wireOp",EDGE,"E9.32.0"),sQuery(id+"F0.wireOp",EDGE,"E9.32.1"),sQuery(id+"F0.wireOp",EDGE,"E9.32.2"),sQuery(id+"F0.wireOp",EDGE,"E9.32.3"),sQuery(id+"F0.wireOp",EDGE,"E9.32.4"),sQuery(id+"F0.wireOp",EDGE,"E9.32.5"),sQuery(id+"F0.wireOp",EDGE,"E9.33.0"),sQuery(id+"F0.wireOp",EDGE,"E9.33.1"),sQuery(id+"F0.wireOp",EDGE,"E9.33.2"),sQuery(id+"F0.wireOp",EDGE,"E9.33.3"),sQuery(id+"F0.wireOp",EDGE,"E9.33.4"),sQuery(id+"F0.wireOp",EDGE,"E9.33.5"),sQuery(id+"F0.wireOp",EDGE,"E9.34.0"),sQuery(id+"F0.wireOp",EDGE,"E9.34.1"),sQuery(id+"F0.wireOp",EDGE,"E9.34.2"),sQuery(id+"F0.wireOp",EDGE,"E9.34.3"),sQuery(id+"F0.wireOp",EDGE,"E9.34.4"),sQuery(id+"F0.wireOp",EDGE,"E9.34.5"),sQuery(id+"F0.wireOp",EDGE,"E9.35.0"),sQuery(id+"F0.wireOp",EDGE,"E9.35.1"),sQuery(id+"F0.wireOp",EDGE,"E9.35.2"),sQuery(id+"F0.wireOp",EDGE,"E9.35.3"),sQuery(id+"F0.wireOp",EDGE,"E9.35.4"),sQuery(id+"F0.wireOp",EDGE,"E9.35.5"),sQuery(id+"F0.wireOp",EDGE,"E9.36.0"),sQuery(id+"F0.wireOp",EDGE,"E9.36.1"),sQuery(id+"F0.wireOp",EDGE,"E9.36.2"),sQuery(id+"F0.wireOp",EDGE,"E9.36.3"),sQuery(id+"F0.wireOp",EDGE,"E9.36.4"),sQuery(id+"F0.wireOp",EDGE,"E9.36.5"),sQuery(id+"F0.wireOp",EDGE,"E9.37.0"),sQuery(id+"F0.wireOp",EDGE,"E9.37.1"),sQuery(id+"F0.wireOp",EDGE,"E9.37.2"),sQuery(id+"F0.wireOp",EDGE,"E9.37.3"),sQuery(id+"F0.wireOp",EDGE,"E9.37.4"),sQuery(id+"F0.wireOp",EDGE,"E9.37.5"),sQuery(id+"F0.wireOp",EDGE,"E9.38.0"),sQuery(id+"F0.wireOp",EDGE,"E9.38.1"),sQuery(id+"F0.wireOp",EDGE,"E9.38.2"),sQuery(id+"F0.wireOp",EDGE,"E9.38.3"),sQuery(id+"F0.wireOp",EDGE,"E9.38.4"),sQuery(id+"F0.wireOp",EDGE,"E9.38.5"),sQuery(id+"F0.wireOp",EDGE,"E9.39.0"),sQuery(id+"F0.wireOp",EDGE,"E9.39.1"),sQuery(id+"F0.wireOp",EDGE,"E9.39.2"),sQuery(id+"F0.wireOp",EDGE,"E9.39.3"),sQuery(id+"F0.wireOp",EDGE,"E9.39.4"),sQuery(id+"F0.wireOp",EDGE,"E9.39.5"),sQuery(id+"F0.wireOp",EDGE,"E9.40.0"),sQuery(id+"F0.wireOp",EDGE,"E9.40.1"),sQuery(id+"F0.wireOp",EDGE,"E9.40.2"),sQuery(id+"F0.wireOp",EDGE,"E9.40.3"),sQuery(id+"F0.wireOp",EDGE,"E9.40.4"),sQuery(id+"F0.wireOp",EDGE,"E9.40.5"),sQuery(id+"F0.wireOp",EDGE,"E9.41.0"),sQuery(id+"F0.wireOp",EDGE,"E9.41.1"),sQuery(id+"F0.wireOp",EDGE,"E9.41.2"),sQuery(id+"F0.wireOp",EDGE,"E9.41.3"),sQuery(id+"F0.wireOp",EDGE,"E9.41.4"),sQuery(id+"F0.wireOp",EDGE,"E9.41.5"),sQuery(id+"F0.wireOp",EDGE,"E9.42.0"),sQuery(id+"F0.wireOp",EDGE,"E9.42.1"),sQuery(id+"F0.wireOp",EDGE,"E9.42.2"),sQuery(id+"F0.wireOp",EDGE,"E9.42.3"),sQuery(id+"F0.wireOp",EDGE,"E9.42.4"),sQuery(id+"F0.wireOp",EDGE,"E9.42.5"),sQuery(id+"F0.wireOp",EDGE,"E9.43.0"),sQuery(id+"F0.wireOp",EDGE,"E9.43.1"),sQuery(id+"F0.wireOp",EDGE,"E9.43.2"),sQuery(id+"F0.wireOp",EDGE,"E9.43.3"),sQuery(id+"F0.wireOp",EDGE,"E9.43.4"),sQuery(id+"F0.wireOp",EDGE,"E9.43.5"),sQuery(id+"F0.wireOp",EDGE,"E9.44.0"),sQuery(id+"F0.wireOp",EDGE,"E9.44.1"),sQuery(id+"F0.wireOp",EDGE,"E9.44.2"),sQuery(id+"F0.wireOp",EDGE,"E9.44.3"),sQuery(id+"F0.wireOp",EDGE,"E9.44.4"),sQuery(id+"F0.wireOp",EDGE,"E9.44.5"),sQuery(id+"F0.wireOp",EDGE,"E9.45.0"),sQuery(id+"F0.wireOp",EDGE,"E9.45.1"),sQuery(id+"F0.wireOp",EDGE,"E9.45.2"),sQuery(id+"F0.wireOp",EDGE,"E9.45.3"),sQuery(id+"F0.wireOp",EDGE,"E9.45.4"),sQuery(id+"F0.wireOp",EDGE,"E9.45.5"),sQuery(id+"F0.wireOp",EDGE,"E9.46.0"),sQuery(id+"F0.wireOp",EDGE,"E9.46.1"),sQuery(id+"F0.wireOp",EDGE,"E9.46.2"),sQuery(id+"F0.wireOp",EDGE,"E9.46.3"),sQuery(id+"F0.wireOp",EDGE,"E9.46.4"),sQuery(id+"F0.wireOp",EDGE,"E9.46.5"),sQuery(id+"F0.wireOp",EDGE,"E9.47.0"),sQuery(id+"F0.wireOp",EDGE,"E9.47.1"),sQuery(id+"F0.wireOp",EDGE,"E9.47.2"),sQuery(id+"F0.wireOp",EDGE,"E9.47.3"),sQuery(id+"F0.wireOp",EDGE,"E9.47.4"),sQuery(id+"F0.wireOp",EDGE,"E9.47.5"),sQuery(id+"F0.wireOp",EDGE,"E10.trimOffspring"),sQuery(id+"F0.wireOp",EDGE,"E11.trimOffspring"),sQuery(id+"F0.wireOp",EDGE,"E12.trimOffspring"),sQuery(id+"F0.wireOp",EDGE,"E13.trimOffspring"),sQuery(id+"F0.wireOp",EDGE,"E14.trimOffspring"),sQuery(id+"F0.wireOp",EDGE,"E15.trimOffspring"),sQuery(id+"F0.wireOp",EDGE,"E16.trimOffspring"),sQuery(id+"F0.wireOp",EDGE,"E17.trimOffspring"),sQuery(id+"F0.wireOp",EDGE,"E18.trimOffspring"),sQuery(id+"F0.wireOp",EDGE,"E19.trimOffspring"),sQuery(id+"F0.wireOp",EDGE,"E20.trimOffspring"),sQuery(id+"F0.wireOp",EDGE,"E21.trimOffspring"),sQuery(id+"F0.wireOp",EDGE,"E22.trimOffspring"),sQuery(id+"F0.wireOp",EDGE,"E23.trimOffspring"),sQuery(id+"F0.wireOp",EDGE,"E24.trimOffspring"),sQuery(id+"F0.wireOp",EDGE,"E25.trimOffspring"),sQuery(id+"F0.wireOp",EDGE,"E26.trimOffspring"),sQuery(id+"F0.wireOp",EDGE,"E27.trimOffspring"),sQuery(id+"F0.wireOp",EDGE,"E28.trimOffspring"),sQuery(id+"F0.wireOp",EDGE,"E29.trimOffspring"),sQuery(id+"F0.wireOp",EDGE,"E30.trimOffspring"),sQuery(id+"F0.wireOp",EDGE,"E31.trimOffspring"),sQuery(id+"F0.wireOp",EDGE,"E32.trimOffspring"),sQuery(id+"F0.wireOp",EDGE,"E33.trimOffspring"),sQuery(id+"F0.wireOp",EDGE,"E34.trimOffspring"),sQuery(id+"F0.wireOp",EDGE,"E35.trimOffspring"),sQuery(id+"F0.wireOp",EDGE,"E36.trimOffspring"),sQuery(id+"F0.wireOp",EDGE,"E37.trimOffspring"),sQuery(id+"F0.wireOp",EDGE,"E38.trimOffspring"),sQuery(id+"F0.wireOp",EDGE,"E39.trimOffspring"),sQuery(id+"F0.wireOp",EDGE,"E40.trimOffspring"),sQuery(id+"F0.wireOp",EDGE,"E41.trimOffspring"),sQuery(id+"F0.wireOp",EDGE,"E42.trimOffspring"),sQuery(id+"F0.wireOp",EDGE,"E43.trimOffspring"),sQuery(id+"F0.wireOp",EDGE,"E44.trimOffspring"),sQuery(id+"F0.wireOp",EDGE,"E45.trimOffspring"),sQuery(id+"F0.wireOp",EDGE,"E46.trimOffspring"),sQuery(id+"F0.wireOp",EDGE,"E47.trimOffspring"),sQuery(id+"F0.wireOp",EDGE,"E48.trimOffspring"),sQuery(id+"F0.wireOp",EDGE,"E49.trimOffspring"),sQuery(id+"F0.wireOp",EDGE,"E50.trimOffspring"),sQuery(id+"F0.wireOp",EDGE,"E51.trimOffspring"),sQuery(id+"F0.wireOp",EDGE,"E52.trimOffspring"),sQuery(id+"F0.wireOp",EDGE,"E53.trimOffspring"),sQuery(id+"F0.wireOp",EDGE,"E54.trimOffspring"),sQuery(id+"F0.wireOp",EDGE,"E55.trimOffspring")])],"isStart":true});
            var sketch = newSketch(context, id + "F4", { "sketchPlane" : qUnion([Q0])});
            skCircle(sketch, "E57", {"center": v(0, 0) * mm, "radius": 15.5 * mm});
            skSolve(sketch);
        }
        {
            var Q0;
            Q0=makeQuery(id+"F4.imprint","IMPRINT",FACE,{"disambiguationData":[TD([[makeQuery(id+"F4.imprint","IMPRINT",EDGE,{"derivedFrom":makeQuery(id+"F1.opExtrude","CAP_EDGE",EDGE,{"disambiguationData":[OSD([sQuery(id+"F0.wireOp",EDGE,"E0")])],"isStart":true})}),-1.0]])]});
            var Q1;
            Q1=makeQuery(id+"F4.imprint","IMPRINT",FACE,{"disambiguationData":[TD([[makeQuery(id+"F4.imprint","IMPRINT",EDGE,{"derivedFrom":sQuery(id+"F4.wireOp",EDGE,"E57")}),1.0]])]});
            extrude(context, id + "F5", {"entities" : qUnion([Q0, Q1]), "operationType" : NewBodyOperationType.ADD, "depth" : .5 * mm, "offsetDistance" : 25 * mm});
        }
        {
            var Q0;
            Q0=makeQuery(id+"F3.opExtrude","CAP_FACE",FACE,{"disambiguationData":[OSD([sQuery(id+"F2.wireOp",EDGE,"E56")])],"isStart":false});
            var sketch = newSketch(context, id + "F6", { "sketchPlane" : qUnion([Q0])});
            skCircle(sketch, "E58", {"center": v(0, 0) * mm, "radius": 1.5 * mm});
            skSolve(sketch);
        }
        {
            var Q0;
            Q0=makeQuery(id+"F6.imprint","IMPRINT",FACE,{"disambiguationData":[TD([[makeQuery(id+"F6.imprint","IMPRINT",EDGE,{"derivedFrom":sQuery(id+"F6.wireOp",EDGE,"E58")}),1.0]])]});
            extrude(context, id + "F7", {"entities" : qUnion([Q0]), "operationType" : NewBodyOperationType.REMOVE, "oppositeDirection" : true, "depth" : 25 * mm, "offsetDistance" : 25 * mm});
        }
    });
